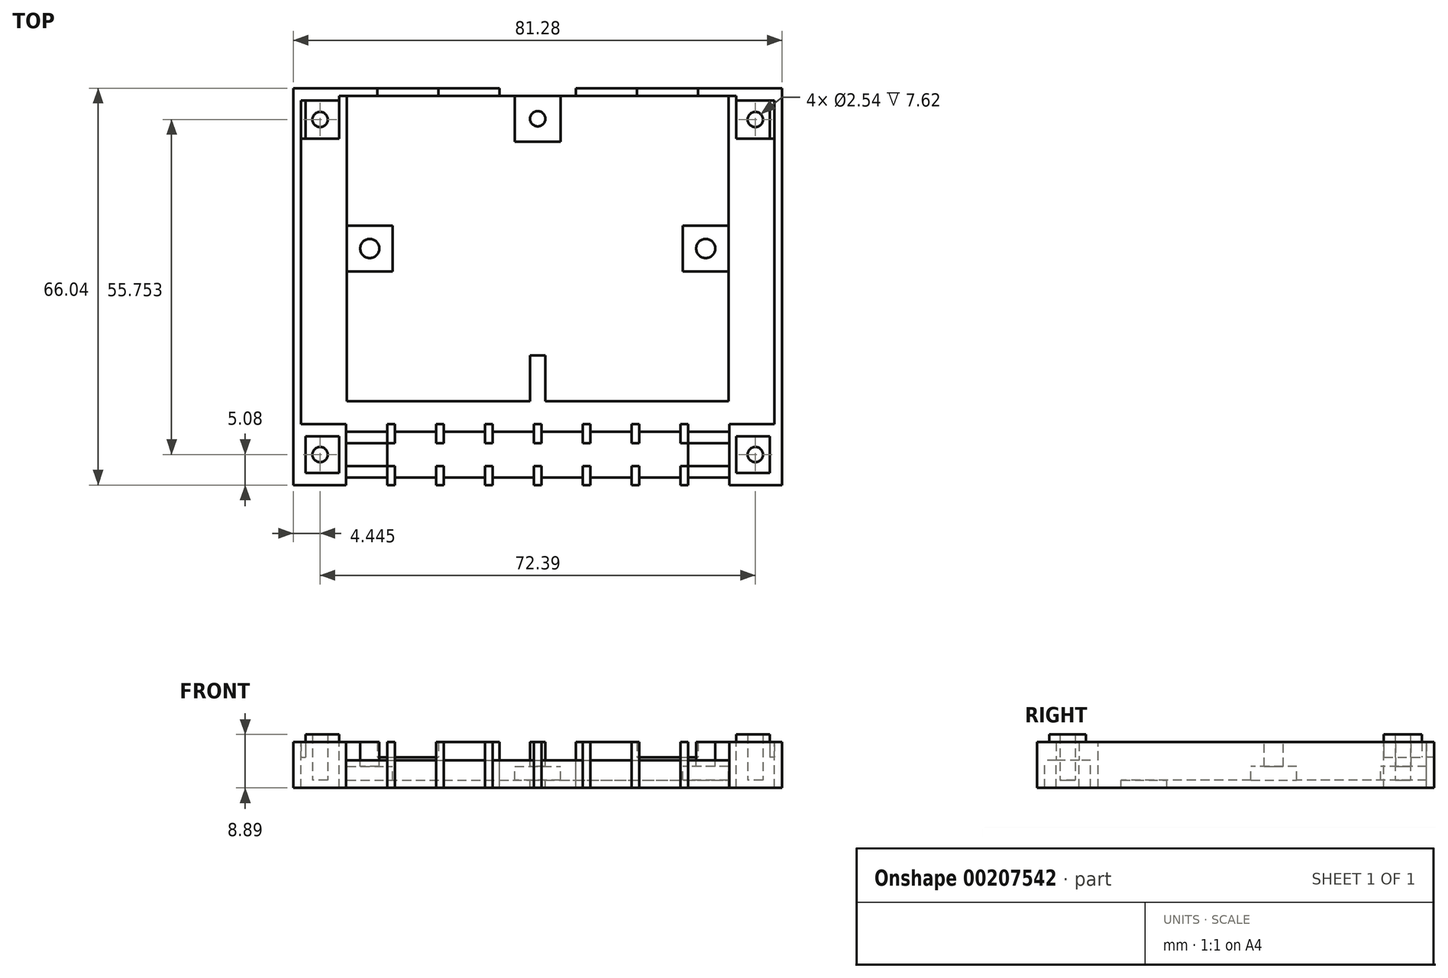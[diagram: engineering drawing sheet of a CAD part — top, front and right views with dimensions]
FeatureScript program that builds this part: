
annotation { "Feature Type Name" : "Feature", "Feature Type Description" : "" }
export const myFeature = defineFeature(function(context is Context, id is Id, definition is map)
    precondition{}
    {
        {
            var Q0;
            Q0=qCreatedBy(makeId("Top.planeOp"),FACE);
            var sketch = newSketch(context, id + "F0", { "sketchPlane" : qUnion([Q0])});
            skLineSegment(sketch, "E0.bottom", {"start": v(-31.75, 25.4) * mm, "end": v(31.75, 25.4) * mm});
            skLineSegment(sketch, "E0.top", {"start": v(-31.75, -25.4) * mm, "end": v(31.75, -25.4) * mm});
            skLineSegment(sketch, "E0.left", {"start": v(-31.75, 25.4) * mm, "end": v(-31.75, -25.4) * mm});
            skLineSegment(sketch, "E0.right", {"start": v(31.75, 25.4) * mm, "end": v(31.75, -25.4) * mm});
            skPoint(sketch, "E0.middle", {"position": v(0, 0) * mm});
            skCircle(sketch, "E1", {"center": v(-27.94, 0) * mm, "radius": 1.59 * mm});
            skCircle(sketch, "E2", {"center": v(27.94, 0) * mm, "radius": 1.59 * mm});
            skCircle(sketch, "E3", {"center": v(0, 21.59) * mm, "radius": 1.27 * mm});
            skLineSegment(sketch, "E4.bottom", {"start": v(-16.51, 32.39) * mm, "end": v(-26.67, 32.38) * mm});
            skLineSegment(sketch, "E4.top", {"start": v(-16.5, 12.07) * mm, "end": v(-26.67, 12.06) * mm});
            skLineSegment(sketch, "E4.left", {"start": v(-16.51, 32.39) * mm, "end": v(-16.5, 12.07) * mm});
            skLineSegment(sketch, "E4.right", {"start": v(-26.67, 32.38) * mm, "end": v(-26.67, 12.06) * mm});
            skPoint(sketch, "E4.middle", {"position": v(-21.59, 22.23) * mm});
            skLineSegment(sketch, "E5.bottom", {"start": v(26.67, 32.39) * mm, "end": v(16.5, 32.39) * mm});
            skLineSegment(sketch, "E5.top", {"start": v(26.67, 12.07) * mm, "end": v(16.5, 12.07) * mm});
            skLineSegment(sketch, "E5.left", {"start": v(26.67, 32.39) * mm, "end": v(26.67, 12.07) * mm});
            skLineSegment(sketch, "E5.right", {"start": v(16.5, 32.38) * mm, "end": v(16.5, 12.07) * mm});
            skPoint(sketch, "E5.middle", {"position": v(21.6, 22.23) * mm});
            skLineSegment(sketch, "E6.bottom", {"start": v(-39.37, 25.4) * mm, "end": v(39.37, 25.4) * mm});
            skLineSegment(sketch, "E6.top", {"start": v(-39.37, -29.21) * mm, "end": v(39.37, -29.21) * mm});
            skLineSegment(sketch, "E6.left", {"start": v(-39.37, 25.4) * mm, "end": v(-39.37, -29.2) * mm});
            skLineSegment(sketch, "E6.right", {"start": v(39.37, 25.4) * mm, "end": v(39.37, -29.2) * mm});
            skLineSegment(sketch, "E7.bottom", {"start": v(-40.64, 26.67) * mm, "end": v(40.64, 26.67) * mm});
            skLineSegment(sketch, "E7.top", {"start": v(-40.64, -39.37) * mm, "end": v(40.64, -39.37) * mm});
            skLineSegment(sketch, "E7.left", {"start": v(-40.64, 26.67) * mm, "end": v(-40.64, -39.37) * mm});
            skLineSegment(sketch, "E7.right", {"start": v(40.64, 26.67) * mm, "end": v(40.64, -39.37) * mm});
            skLineSegment(sketch, "E8.bottom", {"start": v(-39.37, -30.48) * mm, "end": v(39.37, -30.48) * mm});
            skLineSegment(sketch, "E8.top", {"start": v(-39.37, -38.1) * mm, "end": v(39.37, -38.1) * mm});
            skLineSegment(sketch, "E8.left", {"start": v(-39.37, -30.48) * mm, "end": v(-39.37, -38.1) * mm});
            skLineSegment(sketch, "E8.right", {"start": v(39.37, -30.48) * mm, "end": v(39.37, -38.1) * mm});
            skLineSegment(sketch, "E9.bottom", {"start": v(-31.88, -29.21) * mm, "end": v(-25.02, -29.21) * mm});
            skLineSegment(sketch, "E9.top", {"start": v(-31.88, -39.37) * mm, "end": v(-25.02, -39.37) * mm});
            skLineSegment(sketch, "E9.left", {"start": v(-31.88, -29.21) * mm, "end": v(-31.88, -39.37) * mm});
            skLineSegment(sketch, "E9.right", {"start": v(-25.02, -29.21) * mm, "end": v(-25.02, -39.37) * mm});
            skLineSegment(sketch, "E10.1.0.0", {"start": v(-23.75, -29.21) * mm, "end": v(-16.9, -29.21) * mm});
            skLineSegment(sketch, "E10.1.0.1", {"start": v(-23.75, -29.21) * mm, "end": v(-23.75, -39.37) * mm});
            skLineSegment(sketch, "E10.1.0.2", {"start": v(-23.75, -39.37) * mm, "end": v(-16.9, -39.37) * mm});
            skLineSegment(sketch, "E10.1.0.3", {"start": v(-16.9, -29.21) * mm, "end": v(-16.9, -39.37) * mm});
            skLineSegment(sketch, "E10.2.0.0", {"start": v(-15.62, -29.21) * mm, "end": v(-8.76, -29.21) * mm});
            skLineSegment(sketch, "E10.2.0.1", {"start": v(-15.62, -29.21) * mm, "end": v(-15.62, -39.37) * mm});
            skLineSegment(sketch, "E10.2.0.2", {"start": v(-15.62, -39.37) * mm, "end": v(-8.76, -39.37) * mm});
            skLineSegment(sketch, "E10.2.0.3", {"start": v(-8.76, -29.21) * mm, "end": v(-8.76, -39.37) * mm});
            skLineSegment(sketch, "E10.direction1", {"start": v(-31.88, -29.21) * mm, "end": v(-23.75, -29.21) * mm, "construction": true});
            skLineSegment(sketch, "E11.0.3.0", {"start": v(-7.5, -29.21) * mm, "end": v(-0.63, -29.21) * mm});
            skLineSegment(sketch, "E11.3.3.0", {"start": v(-7.5, -29.21) * mm, "end": v(-7.5, -39.37) * mm});
            skLineSegment(sketch, "E11.6.3.0", {"start": v(-7.5, -39.37) * mm, "end": v(-0.64, -39.37) * mm});
            skLineSegment(sketch, "E11.9.3.0", {"start": v(-0.63, -29.21) * mm, "end": v(-0.63, -39.37) * mm});
            skLineSegment(sketch, "E11.0.4.0", {"start": v(0.64, -29.21) * mm, "end": v(7.5, -29.21) * mm});
            skLineSegment(sketch, "E11.3.4.0", {"start": v(0.63, -29.21) * mm, "end": v(0.64, -39.37) * mm});
            skLineSegment(sketch, "E11.6.4.0", {"start": v(0.63, -39.37) * mm, "end": v(7.5, -39.37) * mm});
            skLineSegment(sketch, "E11.9.4.0", {"start": v(7.5, -29.21) * mm, "end": v(7.5, -39.37) * mm});
            skLineSegment(sketch, "E11.0.5.0", {"start": v(8.76, -29.21) * mm, "end": v(15.62, -29.21) * mm});
            skLineSegment(sketch, "E11.3.5.0", {"start": v(8.76, -29.21) * mm, "end": v(8.76, -39.37) * mm});
            skLineSegment(sketch, "E11.6.5.0", {"start": v(8.76, -39.37) * mm, "end": v(15.62, -39.37) * mm});
            skLineSegment(sketch, "E11.9.5.0", {"start": v(15.62, -29.21) * mm, "end": v(15.62, -39.37) * mm});
            skLineSegment(sketch, "E11.0.6.0", {"start": v(16.9, -29.21) * mm, "end": v(23.75, -29.21) * mm});
            skLineSegment(sketch, "E11.3.6.0", {"start": v(16.9, -29.21) * mm, "end": v(16.9, -39.37) * mm});
            skLineSegment(sketch, "E11.6.6.0", {"start": v(16.9, -39.37) * mm, "end": v(23.75, -39.37) * mm});
            skLineSegment(sketch, "E11.9.6.0", {"start": v(23.75, -29.21) * mm, "end": v(23.75, -39.37) * mm});
            skLineSegment(sketch, "E11.0.7.0", {"start": v(25.02, -29.21) * mm, "end": v(31.88, -29.21) * mm});
            skLineSegment(sketch, "E11.3.7.0", {"start": v(25.02, -29.21) * mm, "end": v(25.02, -39.37) * mm});
            skLineSegment(sketch, "E11.6.7.0", {"start": v(25.02, -39.37) * mm, "end": v(31.88, -39.37) * mm});
            skLineSegment(sketch, "E11.9.7.0", {"start": v(31.88, -29.21) * mm, "end": v(31.88, -39.37) * mm});
            skLineSegment(sketch, "E12.bottom", {"start": v(-31.75, -3.8) * mm, "end": v(-24.13, -3.8) * mm});
            skLineSegment(sketch, "E12.top", {"start": v(-31.75, 3.81) * mm, "end": v(-24.13, 3.81) * mm});
            skLineSegment(sketch, "E12.left", {"start": v(-31.75, -3.8) * mm, "end": v(-31.75, 3.81) * mm});
            skLineSegment(sketch, "E12.right", {"start": v(-24.13, -3.8) * mm, "end": v(-24.13, 3.81) * mm});
            skLineSegment(sketch, "E13.bottom", {"start": v(31.75, -3.8) * mm, "end": v(24.13, -3.8) * mm});
            skLineSegment(sketch, "E13.top", {"start": v(31.75, 3.81) * mm, "end": v(24.13, 3.81) * mm});
            skLineSegment(sketch, "E13.left", {"start": v(31.75, -3.8) * mm, "end": v(31.75, 3.81) * mm});
            skLineSegment(sketch, "E13.right", {"start": v(24.13, -3.8) * mm, "end": v(24.13, 3.81) * mm});
            skPoint(sketch, "E13.cornerSnap0", {"position": v(-27.94, -3.8) * mm});
            skLineSegment(sketch, "E14.bottom", {"start": v(3.8, 25.4) * mm, "end": v(-3.81, 25.4) * mm});
            skLineSegment(sketch, "E14.top", {"start": v(3.8, 17.78) * mm, "end": v(-3.81, 17.78) * mm});
            skLineSegment(sketch, "E14.left", {"start": v(3.8, 25.4) * mm, "end": v(3.8, 17.78) * mm});
            skLineSegment(sketch, "E14.right", {"start": v(-3.81, 25.4) * mm, "end": v(-3.81, 17.78) * mm});
            skLineSegment(sketch, "E15.bottom", {"start": v(-1.27, -25.4) * mm, "end": v(1.27, -25.4) * mm});
            skLineSegment(sketch, "E15.top", {"start": v(-1.27, -17.78) * mm, "end": v(1.27, -17.78) * mm});
            skLineSegment(sketch, "E15.left", {"start": v(-1.27, -25.4) * mm, "end": v(-1.27, -17.78) * mm});
            skLineSegment(sketch, "E15.right", {"start": v(1.27, -25.4) * mm, "end": v(1.27, -17.78) * mm});
            skPoint(sketch, "E15.middle", {"position": v(0, -21.59) * mm});
            skCircle(sketch, "E16", {"center": v(-36.2, -34.3) * mm, "radius": 1.27 * mm});
            skCircle(sketch, "E17", {"center": v(36.2, -34.3) * mm, "radius": 1.27 * mm});
            skLineSegment(sketch, "E18.bottom", {"start": v(-31.88, -32.39) * mm, "end": v(31.88, -32.39) * mm});
            skLineSegment(sketch, "E18.top", {"start": v(-31.88, -36.2) * mm, "end": v(31.88, -36.2) * mm});
            skLineSegment(sketch, "E18.left", {"start": v(-31.88, -32.39) * mm, "end": v(-31.88, -36.2) * mm});
            skLineSegment(sketch, "E18.right", {"start": v(31.88, -32.39) * mm, "end": v(31.88, -36.2) * mm});
            skLineSegment(sketch, "E19.bottom", {"start": v(-6.35, 26.67) * mm, "end": v(6.35, 26.67) * mm});
            skLineSegment(sketch, "E19.top", {"start": v(-6.35, 25.4) * mm, "end": v(6.35, 25.4) * mm});
            skLineSegment(sketch, "E19.left", {"start": v(-6.35, 26.67) * mm, "end": v(-6.35, 25.4) * mm});
            skLineSegment(sketch, "E19.right", {"start": v(6.35, 26.67) * mm, "end": v(6.35, 25.4) * mm});
            skLineSegment(sketch, "E20.bottom", {"start": v(-39.37, 24.64) * mm, "end": v(-33.02, 24.64) * mm});
            skLineSegment(sketch, "E20.top", {"start": v(-39.37, 18.29) * mm, "end": v(-33.02, 18.29) * mm});
            skLineSegment(sketch, "E20.left", {"start": v(-39.37, 24.64) * mm, "end": v(-39.37, 18.29) * mm});
            skLineSegment(sketch, "E20.right", {"start": v(-33.02, 24.64) * mm, "end": v(-33.02, 18.29) * mm});
            skLineSegment(sketch, "E21.bottom", {"start": v(39.37, 24.64) * mm, "end": v(33.02, 24.64) * mm});
            skLineSegment(sketch, "E21.top", {"start": v(39.37, 18.29) * mm, "end": v(33.02, 18.29) * mm});
            skLineSegment(sketch, "E21.left", {"start": v(39.37, 24.64) * mm, "end": v(39.37, 18.29) * mm});
            skLineSegment(sketch, "E21.right", {"start": v(33.02, 24.64) * mm, "end": v(33.02, 18.29) * mm});
            skLineSegment(sketch, "E22.bottom", {"start": v(-38.6, -31.24) * mm, "end": v(-33.02, -31.24) * mm});
            skLineSegment(sketch, "E22.top", {"start": v(-38.6, -37.34) * mm, "end": v(-33.02, -37.34) * mm});
            skLineSegment(sketch, "E22.left", {"start": v(-38.6, -31.24) * mm, "end": v(-38.6, -37.34) * mm});
            skLineSegment(sketch, "E22.right", {"start": v(-33.02, -31.24) * mm, "end": v(-33.02, -37.34) * mm});
            skLineSegment(sketch, "E23.bottom", {"start": v(33.02, -31.24) * mm, "end": v(38.6, -31.24) * mm});
            skLineSegment(sketch, "E23.top", {"start": v(33.02, -37.34) * mm, "end": v(38.6, -37.34) * mm});
            skLineSegment(sketch, "E23.left", {"start": v(33.02, -31.24) * mm, "end": v(33.02, -37.34) * mm});
            skLineSegment(sketch, "E23.right", {"start": v(38.6, -31.24) * mm, "end": v(38.6, -37.34) * mm});
            skPoint(sketch, "E24", {"position": v(-36.2, 21.46) * mm});
            skPoint(sketch, "E24.positionSnap0", {"position": v(-39.37, 21.46) * mm});
            skPoint(sketch, "E25", {"position": v(36.2, 21.46) * mm});
            skLineSegment(sketch, "E26", {"start": v(-33.02, 24.64) * mm, "end": v(-33.02, 25.4) * mm});
            skLineSegment(sketch, "E27", {"start": v(33.02, 24.64) * mm, "end": v(33.02, 25.4) * mm});
            skLineSegment(sketch, "E28", {"start": v(-38.6, 18.29) * mm, "end": v(-38.6, 24.64) * mm});
            skLineSegment(sketch, "E29", {"start": v(38.6, 18.29) * mm, "end": v(38.6, 24.64) * mm});
            skCircle(sketch, "E30", {"center": v(-36.2, 21.46) * mm, "radius": 1.27 * mm});
            skCircle(sketch, "E31", {"center": v(36.2, 21.46) * mm, "radius": 1.27 * mm});
            skSolve(sketch);
        }
        {
            var Q0;
            {var subQ0=sQuery(id+"F0.wireOp",EDGE,"E18.bottom");var subQ1=sQuery(id+"F0.wireOp",EDGE,"E11.3.4.0");var subQ2=makeQuery(id+"F0.imprint","INTERSECT",VERTEX,{"derivedFrom":[subQ1,subQ0]});Q0=makeQuery(id+"F0.imprint","IMPRINT",FACE,{"disambiguationData":[TD([[makeQuery(id+"F0.imprint","IMPRINT",EDGE,{"disambiguationData":[TD([[subQ2,-1.0]])],"derivedFrom":subQ1}),1.0]])]});}
            var Q1;
            {var subQ0=sQuery(id+"F0.wireOp",EDGE,"E10.1.0.1");var subQ1=sQuery(id+"F0.wireOp",EDGE,"E8.bottom");var subQ2=makeQuery(id+"F0.imprint","INTERSECT",VERTEX,{"derivedFrom":[subQ1,subQ0]});Q1=makeQuery(id+"F0.imprint","IMPRINT",FACE,{"disambiguationData":[TD([[makeQuery(id+"F0.imprint","IMPRINT",EDGE,{"disambiguationData":[TD([[subQ2,-1.0]])],"derivedFrom":subQ1}),-1.0]])]});}
            var Q2;
            {var subQ5=sQuery(id+"F0.wireOp",EDGE,"E18.right");Q2=makeQuery(id+"F0.imprint","IMPRINT",FACE,{"disambiguationData":[TD([[makeQuery(id+"F0.imprint","IMPRINT",EDGE,{"derivedFrom":subQ5}),-1.0]])]});}
            var Q3;
            {var subQ0=sQuery(id+"F0.wireOp",EDGE,"E11.3.4.0");var subQ1=sQuery(id+"F0.wireOp",EDGE,"E8.top");var subQ2=makeQuery(id+"F0.imprint","INTERSECT",VERTEX,{"derivedFrom":[subQ1,subQ0]});Q3=makeQuery(id+"F0.imprint","IMPRINT",FACE,{"disambiguationData":[TD([[makeQuery(id+"F0.imprint","IMPRINT",EDGE,{"disambiguationData":[TD([[subQ2,-1.0]])],"derivedFrom":subQ1}),1.0]])]});}
            var Q4;
            {var subQ0=sQuery(id+"F0.wireOp",EDGE,"E11.3.3.0");var subQ1=sQuery(id+"F0.wireOp",EDGE,"E8.top");var subQ2=makeQuery(id+"F0.imprint","INTERSECT",VERTEX,{"derivedFrom":[subQ1,subQ0]});Q4=makeQuery(id+"F0.imprint","IMPRINT",FACE,{"disambiguationData":[TD([[makeQuery(id+"F0.imprint","IMPRINT",EDGE,{"disambiguationData":[TD([[subQ2,-1.0]])],"derivedFrom":subQ1}),1.0]])]});}
            var Q5;
            {var subQ0=sQuery(id+"F0.wireOp",EDGE,"E18.bottom");var subQ1=sQuery(id+"F0.wireOp",EDGE,"E11.9.3.0");var subQ2=makeQuery(id+"F0.imprint","INTERSECT",VERTEX,{"derivedFrom":[subQ1,subQ0]});Q5=makeQuery(id+"F0.imprint","IMPRINT",FACE,{"disambiguationData":[TD([[makeQuery(id+"F0.imprint","IMPRINT",EDGE,{"disambiguationData":[TD([[subQ2,-1.0]])],"derivedFrom":subQ1}),1.0]])]});}
            var Q6;
            {var subQ0=sQuery(id+"F0.wireOp",EDGE,"E11.3.4.0");var subQ1=sQuery(id+"F0.wireOp",EDGE,"E8.bottom");var subQ2=makeQuery(id+"F0.imprint","INTERSECT",VERTEX,{"derivedFrom":[subQ1,subQ0]});Q6=makeQuery(id+"F0.imprint","IMPRINT",FACE,{"disambiguationData":[TD([[makeQuery(id+"F0.imprint","IMPRINT",EDGE,{"disambiguationData":[TD([[subQ2,-1.0]])],"derivedFrom":subQ1}),-1.0]])]});}
            var Q7;
            {var subQ0=sQuery(id+"F0.wireOp",EDGE,"E18.bottom");var subQ1=sQuery(id+"F0.wireOp",EDGE,"E11.3.3.0");var subQ2=makeQuery(id+"F0.imprint","INTERSECT",VERTEX,{"derivedFrom":[subQ1,subQ0]});Q7=makeQuery(id+"F0.imprint","IMPRINT",FACE,{"disambiguationData":[TD([[makeQuery(id+"F0.imprint","IMPRINT",EDGE,{"disambiguationData":[TD([[subQ2,-1.0]])],"derivedFrom":subQ1}),1.0]])]});}
            var Q8;
            {var subQ0=sQuery(id+"F0.wireOp",EDGE,"E5.top");Q8=makeQuery(id+"F0.imprint","IMPRINT",FACE,{"disambiguationData":[TD([[makeQuery(id+"F0.imprint","IMPRINT",EDGE,{"derivedFrom":subQ0}),-1.0]])]});}
            var Q9;
            {var subQ0=sQuery(id+"F0.wireOp",EDGE,"E4.top");Q9=makeQuery(id+"F0.imprint","IMPRINT",FACE,{"disambiguationData":[TD([[makeQuery(id+"F0.imprint","IMPRINT",EDGE,{"derivedFrom":subQ0}),-1.0]])]});}
            var Q10;
            Q10=makeQuery(id+"F0.imprint","IMPRINT",FACE,{"disambiguationData":[TD([[makeQuery(id+"F0.imprint","IMPRINT",EDGE,{"derivedFrom":sQuery(id+"F0.wireOp",EDGE,"E1")}),-1.0]])]});
            var Q11;
            Q11=makeQuery(id+"F0.imprint","IMPRINT",FACE,{"disambiguationData":[TD([[makeQuery(id+"F0.imprint","IMPRINT",EDGE,{"derivedFrom":sQuery(id+"F0.wireOp",EDGE,"E2")}),-1.0]])]});
            var Q12;
            {var subQ0=sQuery(id+"F0.wireOp",EDGE,"E10.2.0.1");var subQ1=sQuery(id+"F0.wireOp",EDGE,"E8.top");var subQ2=makeQuery(id+"F0.imprint","INTERSECT",VERTEX,{"derivedFrom":[subQ1,subQ0]});Q12=makeQuery(id+"F0.imprint","IMPRINT",FACE,{"disambiguationData":[TD([[makeQuery(id+"F0.imprint","IMPRINT",EDGE,{"disambiguationData":[TD([[subQ2,-1.0]])],"derivedFrom":subQ1}),1.0]])]});}
            var Q13;
            {var subQ23=sQuery(id+"F0.wireOp",EDGE,"E4.top");Q13=makeQuery(id+"F0.imprint","IMPRINT",FACE,{"disambiguationData":[TD([[makeQuery(id+"F0.imprint","IMPRINT",EDGE,{"derivedFrom":subQ23}),1.0]])]});}
            var Q14;
            {var subQ0=sQuery(id+"F0.wireOp",EDGE,"E11.3.3.0");var subQ1=sQuery(id+"F0.wireOp",EDGE,"E8.bottom");var subQ2=makeQuery(id+"F0.imprint","INTERSECT",VERTEX,{"derivedFrom":[subQ1,subQ0]});Q14=makeQuery(id+"F0.imprint","IMPRINT",FACE,{"disambiguationData":[TD([[makeQuery(id+"F0.imprint","IMPRINT",EDGE,{"disambiguationData":[TD([[subQ2,-1.0]])],"derivedFrom":subQ1}),-1.0]])]});}
            var Q15;
            {var subQ0=sQuery(id+"F0.wireOp",EDGE,"E10.1.0.3");var subQ1=sQuery(id+"F0.wireOp",EDGE,"E8.top");var subQ2=makeQuery(id+"F0.imprint","INTERSECT",VERTEX,{"derivedFrom":[subQ1,subQ0]});Q15=makeQuery(id+"F0.imprint","IMPRINT",FACE,{"disambiguationData":[TD([[makeQuery(id+"F0.imprint","IMPRINT",EDGE,{"disambiguationData":[TD([[subQ2,-1.0]])],"derivedFrom":subQ1}),1.0]])]});}
            var Q16;
            {var subQ0=sQuery(id+"F0.wireOp",EDGE,"E18.bottom");var subQ1=sQuery(id+"F0.wireOp",EDGE,"E10.2.0.1");var subQ2=makeQuery(id+"F0.imprint","INTERSECT",VERTEX,{"derivedFrom":[subQ1,subQ0]});Q16=makeQuery(id+"F0.imprint","IMPRINT",FACE,{"disambiguationData":[TD([[makeQuery(id+"F0.imprint","IMPRINT",EDGE,{"disambiguationData":[TD([[subQ2,-1.0]])],"derivedFrom":subQ1}),1.0]])]});}
            var Q17;
            {var subQ11=sQuery(id+"F0.wireOp",EDGE,"E7.right");Q17=makeQuery(id+"F0.imprint","IMPRINT",FACE,{"disambiguationData":[TD([[makeQuery(id+"F0.imprint","IMPRINT",EDGE,{"derivedFrom":subQ11}),-1.0]])]});}
            var Q18;
            {var subQ0=sQuery(id+"F0.wireOp",EDGE,"E10.1.0.1");var subQ1=sQuery(id+"F0.wireOp",EDGE,"E8.top");var subQ2=makeQuery(id+"F0.imprint","INTERSECT",VERTEX,{"derivedFrom":[subQ1,subQ0]});Q18=makeQuery(id+"F0.imprint","IMPRINT",FACE,{"disambiguationData":[TD([[makeQuery(id+"F0.imprint","IMPRINT",EDGE,{"disambiguationData":[TD([[subQ2,-1.0]])],"derivedFrom":subQ1}),1.0]])]});}
            var Q19;
            {var subQ0=sQuery(id+"F0.wireOp",EDGE,"E18.bottom");var subQ1=sQuery(id+"F0.wireOp",EDGE,"E10.1.0.1");var subQ2=makeQuery(id+"F0.imprint","INTERSECT",VERTEX,{"derivedFrom":[subQ1,subQ0]});Q19=makeQuery(id+"F0.imprint","IMPRINT",FACE,{"disambiguationData":[TD([[makeQuery(id+"F0.imprint","IMPRINT",EDGE,{"disambiguationData":[TD([[subQ2,-1.0]])],"derivedFrom":subQ1}),1.0]])]});}
            var Q20;
            {var subQ0=sQuery(id+"F0.wireOp",EDGE,"E8.right");Q20=makeQuery(id+"F0.imprint","IMPRINT",FACE,{"disambiguationData":[TD([[makeQuery(id+"F0.imprint","IMPRINT",EDGE,{"derivedFrom":subQ0}),-1.0]])]});}
            var Q21;
            {var subQ0=sQuery(id+"F0.wireOp",EDGE,"E10.2.0.1");var subQ1=sQuery(id+"F0.wireOp",EDGE,"E8.bottom");var subQ2=makeQuery(id+"F0.imprint","INTERSECT",VERTEX,{"derivedFrom":[subQ1,subQ0]});Q21=makeQuery(id+"F0.imprint","IMPRINT",FACE,{"disambiguationData":[TD([[makeQuery(id+"F0.imprint","IMPRINT",EDGE,{"disambiguationData":[TD([[subQ2,-1.0]])],"derivedFrom":subQ1}),-1.0]])]});}
            var Q22;
            {var subQ5=sQuery(id+"F0.wireOp",EDGE,"E11.6.5.0");Q22=makeQuery(id+"F0.imprint","IMPRINT",FACE,{"disambiguationData":[TD([[makeQuery(id+"F0.imprint","IMPRINT",EDGE,{"derivedFrom":subQ5}),1.0]])]});}
            var Q23;
            {var subQ5=sQuery(id+"F0.wireOp",EDGE,"E11.6.7.0");Q23=makeQuery(id+"F0.imprint","IMPRINT",FACE,{"disambiguationData":[TD([[makeQuery(id+"F0.imprint","IMPRINT",EDGE,{"derivedFrom":subQ5}),1.0]])]});}
            var Q24;
            {var subQ0=sQuery(id+"F0.wireOp",EDGE,"E11.3.7.0");var subQ1=sQuery(id+"F0.wireOp",EDGE,"E8.bottom");var subQ2=makeQuery(id+"F0.imprint","INTERSECT",VERTEX,{"derivedFrom":[subQ1,subQ0]});Q24=makeQuery(id+"F0.imprint","IMPRINT",FACE,{"disambiguationData":[TD([[makeQuery(id+"F0.imprint","IMPRINT",EDGE,{"disambiguationData":[TD([[subQ2,-1.0]])],"derivedFrom":subQ1}),-1.0]])]});}
            var Q25;
            {var subQ0=sQuery(id+"F0.wireOp",EDGE,"E18.bottom");var subQ1=sQuery(id+"F0.wireOp",EDGE,"E9.right");var subQ2=makeQuery(id+"F0.imprint","INTERSECT",VERTEX,{"derivedFrom":[subQ1,subQ0]});Q25=makeQuery(id+"F0.imprint","IMPRINT",FACE,{"disambiguationData":[TD([[makeQuery(id+"F0.imprint","IMPRINT",EDGE,{"disambiguationData":[TD([[subQ2,-1.0]])],"derivedFrom":subQ1}),1.0]])]});}
            var Q26;
            {var subQ5=sQuery(id+"F0.wireOp",EDGE,"E11.6.6.0");Q26=makeQuery(id+"F0.imprint","IMPRINT",FACE,{"disambiguationData":[TD([[makeQuery(id+"F0.imprint","IMPRINT",EDGE,{"derivedFrom":subQ5}),1.0]])]});}
            var Q27;
            Q27=makeQuery(id+"F0.imprint","IMPRINT",FACE,{"disambiguationData":[TD([[makeQuery(id+"F0.imprint","IMPRINT",EDGE,{"derivedFrom":sQuery(id+"F0.wireOp",EDGE,"E3")}),-1.0]])]});
            var Q28;
            {var subQ0=sQuery(id+"F0.wireOp",EDGE,"E11.3.7.0");var subQ1=sQuery(id+"F0.wireOp",EDGE,"E8.top");var subQ2=makeQuery(id+"F0.imprint","INTERSECT",VERTEX,{"derivedFrom":[subQ1,subQ0]});Q28=makeQuery(id+"F0.imprint","IMPRINT",FACE,{"disambiguationData":[TD([[makeQuery(id+"F0.imprint","IMPRINT",EDGE,{"disambiguationData":[TD([[subQ2,-1.0]])],"derivedFrom":subQ1}),1.0]])]});}
            var Q29;
            {var subQ0=sQuery(id+"F0.wireOp",EDGE,"E11.3.5.0");var subQ1=sQuery(id+"F0.wireOp",EDGE,"E8.top");var subQ2=makeQuery(id+"F0.imprint","INTERSECT",VERTEX,{"derivedFrom":[subQ1,subQ0]});Q29=makeQuery(id+"F0.imprint","IMPRINT",FACE,{"disambiguationData":[TD([[makeQuery(id+"F0.imprint","IMPRINT",EDGE,{"disambiguationData":[TD([[subQ2,-1.0]])],"derivedFrom":subQ1}),1.0]])]});}
            var Q30;
            {var subQ0=sQuery(id+"F0.wireOp",EDGE,"E18.bottom");var subQ1=sQuery(id+"F0.wireOp",EDGE,"E11.9.5.0");var subQ2=makeQuery(id+"F0.imprint","INTERSECT",VERTEX,{"derivedFrom":[subQ1,subQ0]});Q30=makeQuery(id+"F0.imprint","IMPRINT",FACE,{"disambiguationData":[TD([[makeQuery(id+"F0.imprint","IMPRINT",EDGE,{"disambiguationData":[TD([[subQ2,-1.0]])],"derivedFrom":subQ1}),1.0]])]});}
            var Q31;
            {var subQ5=sQuery(id+"F0.wireOp",EDGE,"E10.2.0.2");Q31=makeQuery(id+"F0.imprint","IMPRINT",FACE,{"disambiguationData":[TD([[makeQuery(id+"F0.imprint","IMPRINT",EDGE,{"derivedFrom":subQ5}),1.0]])]});}
            var Q32;
            {var subQ0=sQuery(id+"F0.wireOp",EDGE,"E9.left");var subQ1=sQuery(id+"F0.wireOp",EDGE,"E8.bottom");var subQ2=makeQuery(id+"F0.imprint","INTERSECT",VERTEX,{"derivedFrom":[subQ1,subQ0]});Q32=makeQuery(id+"F0.imprint","IMPRINT",FACE,{"disambiguationData":[TD([[makeQuery(id+"F0.imprint","IMPRINT",EDGE,{"disambiguationData":[TD([[subQ2,-1.0]])],"derivedFrom":subQ1}),-1.0]])]});}
            var Q33;
            {var subQ5=sQuery(id+"F0.wireOp",EDGE,"E11.6.4.0");Q33=makeQuery(id+"F0.imprint","IMPRINT",FACE,{"disambiguationData":[TD([[makeQuery(id+"F0.imprint","IMPRINT",EDGE,{"derivedFrom":subQ5}),1.0]])]});}
            var Q34;
            {var subQ0=sQuery(id+"F0.wireOp",EDGE,"E11.3.6.0");var subQ1=sQuery(id+"F0.wireOp",EDGE,"E8.bottom");var subQ2=makeQuery(id+"F0.imprint","INTERSECT",VERTEX,{"derivedFrom":[subQ1,subQ0]});Q34=makeQuery(id+"F0.imprint","IMPRINT",FACE,{"disambiguationData":[TD([[makeQuery(id+"F0.imprint","IMPRINT",EDGE,{"disambiguationData":[TD([[subQ2,-1.0]])],"derivedFrom":subQ1}),-1.0]])]});}
            var Q35;
            {var subQ0=sQuery(id+"F0.wireOp",EDGE,"E11.3.6.0");var subQ1=sQuery(id+"F0.wireOp",EDGE,"E8.top");var subQ2=makeQuery(id+"F0.imprint","INTERSECT",VERTEX,{"derivedFrom":[subQ1,subQ0]});Q35=makeQuery(id+"F0.imprint","IMPRINT",FACE,{"disambiguationData":[TD([[makeQuery(id+"F0.imprint","IMPRINT",EDGE,{"disambiguationData":[TD([[subQ2,-1.0]])],"derivedFrom":subQ1}),1.0]])]});}
            var Q36;
            {var subQ0=sQuery(id+"F0.wireOp",EDGE,"E18.bottom");var subQ1=sQuery(id+"F0.wireOp",EDGE,"E11.3.5.0");var subQ2=makeQuery(id+"F0.imprint","INTERSECT",VERTEX,{"derivedFrom":[subQ1,subQ0]});Q36=makeQuery(id+"F0.imprint","IMPRINT",FACE,{"disambiguationData":[TD([[makeQuery(id+"F0.imprint","IMPRINT",EDGE,{"disambiguationData":[TD([[subQ2,-1.0]])],"derivedFrom":subQ1}),1.0]])]});}
            var Q37;
            {var subQ5=sQuery(id+"F0.wireOp",EDGE,"E10.1.0.2");Q37=makeQuery(id+"F0.imprint","IMPRINT",FACE,{"disambiguationData":[TD([[makeQuery(id+"F0.imprint","IMPRINT",EDGE,{"derivedFrom":subQ5}),1.0]])]});}
            var Q38;
            {var subQ5=sQuery(id+"F0.wireOp",EDGE,"E9.bottom");Q38=makeQuery(id+"F0.imprint","IMPRINT",FACE,{"disambiguationData":[TD([[makeQuery(id+"F0.imprint","IMPRINT",EDGE,{"derivedFrom":subQ5}),-1.0]])]});}
            var Q39;
            {var subQ0=sQuery(id+"F0.wireOp",EDGE,"E11.3.5.0");var subQ1=sQuery(id+"F0.wireOp",EDGE,"E8.bottom");var subQ2=makeQuery(id+"F0.imprint","INTERSECT",VERTEX,{"derivedFrom":[subQ1,subQ0]});Q39=makeQuery(id+"F0.imprint","IMPRINT",FACE,{"disambiguationData":[TD([[makeQuery(id+"F0.imprint","IMPRINT",EDGE,{"disambiguationData":[TD([[subQ2,-1.0]])],"derivedFrom":subQ1}),-1.0]])]});}
            var Q40;
            {var subQ0=sQuery(id+"F0.wireOp",EDGE,"E18.bottom");var subQ1=sQuery(id+"F0.wireOp",EDGE,"E11.3.6.0");var subQ2=makeQuery(id+"F0.imprint","INTERSECT",VERTEX,{"derivedFrom":[subQ1,subQ0]});Q40=makeQuery(id+"F0.imprint","IMPRINT",FACE,{"disambiguationData":[TD([[makeQuery(id+"F0.imprint","IMPRINT",EDGE,{"disambiguationData":[TD([[subQ2,-1.0]])],"derivedFrom":subQ1}),1.0]])]});}
            var Q41;
            {var subQ5=sQuery(id+"F0.wireOp",EDGE,"E11.6.3.0");Q41=makeQuery(id+"F0.imprint","IMPRINT",FACE,{"disambiguationData":[TD([[makeQuery(id+"F0.imprint","IMPRINT",EDGE,{"derivedFrom":subQ5}),1.0]])]});}
            var Q42;
            {var subQ5=sQuery(id+"F0.wireOp",EDGE,"E11.0.5.0");Q42=makeQuery(id+"F0.imprint","IMPRINT",FACE,{"disambiguationData":[TD([[makeQuery(id+"F0.imprint","IMPRINT",EDGE,{"derivedFrom":subQ5}),-1.0]])]});}
            var Q43;
            {var subQ0=sQuery(id+"F0.wireOp",EDGE,"E18.bottom");var subQ1=sQuery(id+"F0.wireOp",EDGE,"E11.9.4.0");var subQ2=makeQuery(id+"F0.imprint","INTERSECT",VERTEX,{"derivedFrom":[subQ1,subQ0]});Q43=makeQuery(id+"F0.imprint","IMPRINT",FACE,{"disambiguationData":[TD([[makeQuery(id+"F0.imprint","IMPRINT",EDGE,{"disambiguationData":[TD([[subQ2,-1.0]])],"derivedFrom":subQ1}),1.0]])]});}
            var Q44;
            {var subQ0=sQuery(id+"F0.wireOp",EDGE,"E11.9.3.0");var subQ1=sQuery(id+"F0.wireOp",EDGE,"E8.top");var subQ2=makeQuery(id+"F0.imprint","INTERSECT",VERTEX,{"derivedFrom":[subQ1,subQ0]});Q44=makeQuery(id+"F0.imprint","IMPRINT",FACE,{"disambiguationData":[TD([[makeQuery(id+"F0.imprint","IMPRINT",EDGE,{"disambiguationData":[TD([[subQ2,-1.0]])],"derivedFrom":subQ1}),1.0]])]});}
            var Q45;
            {var subQ0=sQuery(id+"F0.wireOp",EDGE,"E11.9.6.0");var subQ1=sQuery(id+"F0.wireOp",EDGE,"E8.bottom");var subQ2=makeQuery(id+"F0.imprint","INTERSECT",VERTEX,{"derivedFrom":[subQ1,subQ0]});Q45=makeQuery(id+"F0.imprint","IMPRINT",FACE,{"disambiguationData":[TD([[makeQuery(id+"F0.imprint","IMPRINT",EDGE,{"disambiguationData":[TD([[subQ2,-1.0]])],"derivedFrom":subQ1}),-1.0]])]});}
            var Q46;
            {var subQ5=sQuery(id+"F0.wireOp",EDGE,"E11.0.4.0");Q46=makeQuery(id+"F0.imprint","IMPRINT",FACE,{"disambiguationData":[TD([[makeQuery(id+"F0.imprint","IMPRINT",EDGE,{"derivedFrom":subQ5}),-1.0]])]});}
            var Q47;
            Q47=makeQuery(id+"F0.imprint","IMPRINT",FACE,{"disambiguationData":[TD([[makeQuery(id+"F0.imprint","IMPRINT",EDGE,{"derivedFrom":sQuery(id+"F0.wireOp",EDGE,"y6P8BbUv-Oivx-0iiG-fBJo-7x3XaV8NzKCm.bottom")}),-1.0]])]});
            var Q48;
            Q48=makeQuery(id+"F0.imprint","IMPRINT",FACE,{"disambiguationData":[TD([[makeQuery(id+"F0.imprint","IMPRINT",EDGE,{"derivedFrom":sQuery(id+"F0.wireOp",EDGE,"E20.bottom")}),-1.0]])]});
            var Q49;
            Q49=makeQuery(id+"F0.imprint","IMPRINT",FACE,{"disambiguationData":[TD([[makeQuery(id+"F0.imprint","IMPRINT",EDGE,{"derivedFrom":sQuery(id+"F0.wireOp",EDGE,"E15.bottom")}),1.0]])]});
            var Q50;
            Q50=makeQuery(id+"F0.imprint","IMPRINT",FACE,{"disambiguationData":[TD([[makeQuery(id+"F0.imprint","IMPRINT",EDGE,{"derivedFrom":sQuery(id+"F0.wireOp",EDGE,"E21.bottom")}),1.0]])]});
            var Q51;
            {var subQ0=sQuery(id+"F0.wireOp",EDGE,"E11.9.3.0");var subQ1=sQuery(id+"F0.wireOp",EDGE,"E8.bottom");var subQ2=makeQuery(id+"F0.imprint","INTERSECT",VERTEX,{"derivedFrom":[subQ1,subQ0]});Q51=makeQuery(id+"F0.imprint","IMPRINT",FACE,{"disambiguationData":[TD([[makeQuery(id+"F0.imprint","IMPRINT",EDGE,{"disambiguationData":[TD([[subQ2,-1.0]])],"derivedFrom":subQ1}),-1.0]])]});}
            var Q52;
            {var subQ0=sQuery(id+"F0.wireOp",EDGE,"E18.bottom");var subQ1=sQuery(id+"F0.wireOp",EDGE,"E10.2.0.3");var subQ2=makeQuery(id+"F0.imprint","INTERSECT",VERTEX,{"derivedFrom":[subQ1,subQ0]});Q52=makeQuery(id+"F0.imprint","IMPRINT",FACE,{"disambiguationData":[TD([[makeQuery(id+"F0.imprint","IMPRINT",EDGE,{"disambiguationData":[TD([[subQ2,-1.0]])],"derivedFrom":subQ1}),1.0]])]});}
            var Q53;
            {var subQ0=sQuery(id+"F0.wireOp",EDGE,"E11.9.5.0");var subQ1=sQuery(id+"F0.wireOp",EDGE,"E8.top");var subQ2=makeQuery(id+"F0.imprint","INTERSECT",VERTEX,{"derivedFrom":[subQ1,subQ0]});Q53=makeQuery(id+"F0.imprint","IMPRINT",FACE,{"disambiguationData":[TD([[makeQuery(id+"F0.imprint","IMPRINT",EDGE,{"disambiguationData":[TD([[subQ2,-1.0]])],"derivedFrom":subQ1}),1.0]])]});}
            var Q54;
            {var subQ5=sQuery(id+"F0.wireOp",EDGE,"E11.0.3.0");Q54=makeQuery(id+"F0.imprint","IMPRINT",FACE,{"disambiguationData":[TD([[makeQuery(id+"F0.imprint","IMPRINT",EDGE,{"derivedFrom":subQ5}),-1.0]])]});}
            var Q55;
            {var subQ0=sQuery(id+"F0.wireOp",EDGE,"E18.bottom");var subQ1=sQuery(id+"F0.wireOp",EDGE,"E10.1.0.3");var subQ2=makeQuery(id+"F0.imprint","INTERSECT",VERTEX,{"derivedFrom":[subQ1,subQ0]});Q55=makeQuery(id+"F0.imprint","IMPRINT",FACE,{"disambiguationData":[TD([[makeQuery(id+"F0.imprint","IMPRINT",EDGE,{"disambiguationData":[TD([[subQ2,-1.0]])],"derivedFrom":subQ1}),1.0]])]});}
            var Q56;
            {var subQ0=sQuery(id+"F0.wireOp",EDGE,"E7.bottom");var subQ1=sQuery(id+"F0.wireOp",EDGE,"E5.left");var subQ2=makeQuery(id+"F0.imprint","INTERSECT",VERTEX,{"derivedFrom":[subQ1,subQ0]});Q56=makeQuery(id+"F0.imprint","IMPRINT",FACE,{"disambiguationData":[TD([[makeQuery(id+"F0.imprint","IMPRINT",EDGE,{"disambiguationData":[TD([[subQ2,-1.0]])],"derivedFrom":subQ1}),-1.0]])]});}
            var Q57;
            {var subQ0=sQuery(id+"F0.wireOp",EDGE,"E9.right");var subQ1=sQuery(id+"F0.wireOp",EDGE,"E8.top");var subQ2=makeQuery(id+"F0.imprint","INTERSECT",VERTEX,{"derivedFrom":[subQ1,subQ0]});Q57=makeQuery(id+"F0.imprint","IMPRINT",FACE,{"disambiguationData":[TD([[makeQuery(id+"F0.imprint","IMPRINT",EDGE,{"disambiguationData":[TD([[subQ2,-1.0]])],"derivedFrom":subQ1}),1.0]])]});}
            var Q58;
            {var subQ0=sQuery(id+"F0.wireOp",EDGE,"E7.bottom");var subQ1=sQuery(id+"F0.wireOp",EDGE,"E4.left");var subQ2=makeQuery(id+"F0.imprint","INTERSECT",VERTEX,{"derivedFrom":[subQ1,subQ0]});Q58=makeQuery(id+"F0.imprint","IMPRINT",FACE,{"disambiguationData":[TD([[makeQuery(id+"F0.imprint","IMPRINT",EDGE,{"disambiguationData":[TD([[subQ2,-1.0]])],"derivedFrom":subQ1}),-1.0]])]});}
            var Q59;
            {var subQ5=sQuery(id+"F0.wireOp",EDGE,"E19.right");Q59=makeQuery(id+"F0.imprint","IMPRINT",FACE,{"disambiguationData":[TD([[makeQuery(id+"F0.imprint","IMPRINT",EDGE,{"derivedFrom":subQ5}),1.0]])]});}
            var Q60;
            {var subQ5=sQuery(id+"F0.wireOp",EDGE,"E10.2.0.0");Q60=makeQuery(id+"F0.imprint","IMPRINT",FACE,{"disambiguationData":[TD([[makeQuery(id+"F0.imprint","IMPRINT",EDGE,{"derivedFrom":subQ5}),-1.0]])]});}
            var Q61;
            {var subQ5=sQuery(id+"F0.wireOp",EDGE,"E19.left");Q61=makeQuery(id+"F0.imprint","IMPRINT",FACE,{"disambiguationData":[TD([[makeQuery(id+"F0.imprint","IMPRINT",EDGE,{"derivedFrom":subQ5}),-1.0]])]});}
            var Q62;
            Q62=makeQuery(id+"F0.imprint","IMPRINT",FACE,{"disambiguationData":[TD([[makeQuery(id+"F0.imprint","IMPRINT",EDGE,{"derivedFrom":sQuery(id+"F0.wireOp",EDGE,"E19.bottom")}),-1.0]])]});
            var Q63;
            {var subQ5=sQuery(id+"F0.wireOp",EDGE,"E11.0.7.0");Q63=makeQuery(id+"F0.imprint","IMPRINT",FACE,{"disambiguationData":[TD([[makeQuery(id+"F0.imprint","IMPRINT",EDGE,{"derivedFrom":subQ5}),-1.0]])]});}
            var Q64;
            {var subQ0=sQuery(id+"F0.wireOp",EDGE,"E11.9.5.0");var subQ1=sQuery(id+"F0.wireOp",EDGE,"E8.bottom");var subQ2=makeQuery(id+"F0.imprint","INTERSECT",VERTEX,{"derivedFrom":[subQ1,subQ0]});Q64=makeQuery(id+"F0.imprint","IMPRINT",FACE,{"disambiguationData":[TD([[makeQuery(id+"F0.imprint","IMPRINT",EDGE,{"disambiguationData":[TD([[subQ2,-1.0]])],"derivedFrom":subQ1}),-1.0]])]});}
            var Q65;
            {var subQ0=sQuery(id+"F0.wireOp",EDGE,"E18.bottom");var subQ1=sQuery(id+"F0.wireOp",EDGE,"E11.9.6.0");var subQ2=makeQuery(id+"F0.imprint","INTERSECT",VERTEX,{"derivedFrom":[subQ1,subQ0]});Q65=makeQuery(id+"F0.imprint","IMPRINT",FACE,{"disambiguationData":[TD([[makeQuery(id+"F0.imprint","IMPRINT",EDGE,{"disambiguationData":[TD([[subQ2,-1.0]])],"derivedFrom":subQ1}),1.0]])]});}
            var Q66;
            {var subQ5=sQuery(id+"F0.wireOp",EDGE,"E10.1.0.0");Q66=makeQuery(id+"F0.imprint","IMPRINT",FACE,{"disambiguationData":[TD([[makeQuery(id+"F0.imprint","IMPRINT",EDGE,{"derivedFrom":subQ5}),-1.0]])]});}
            var Q67;
            {var subQ0=sQuery(id+"F0.wireOp",EDGE,"E9.right");var subQ1=sQuery(id+"F0.wireOp",EDGE,"E8.bottom");var subQ2=makeQuery(id+"F0.imprint","INTERSECT",VERTEX,{"derivedFrom":[subQ1,subQ0]});Q67=makeQuery(id+"F0.imprint","IMPRINT",FACE,{"disambiguationData":[TD([[makeQuery(id+"F0.imprint","IMPRINT",EDGE,{"disambiguationData":[TD([[subQ2,-1.0]])],"derivedFrom":subQ1}),-1.0]])]});}
            var Q68;
            {var subQ5=sQuery(id+"F0.wireOp",EDGE,"E11.0.6.0");Q68=makeQuery(id+"F0.imprint","IMPRINT",FACE,{"disambiguationData":[TD([[makeQuery(id+"F0.imprint","IMPRINT",EDGE,{"derivedFrom":subQ5}),-1.0]])]});}
            var Q69;
            {var subQ0=sQuery(id+"F0.wireOp",EDGE,"E11.9.6.0");var subQ1=sQuery(id+"F0.wireOp",EDGE,"E8.top");var subQ2=makeQuery(id+"F0.imprint","INTERSECT",VERTEX,{"derivedFrom":[subQ1,subQ0]});Q69=makeQuery(id+"F0.imprint","IMPRINT",FACE,{"disambiguationData":[TD([[makeQuery(id+"F0.imprint","IMPRINT",EDGE,{"disambiguationData":[TD([[subQ2,-1.0]])],"derivedFrom":subQ1}),1.0]])]});}
            var Q70;
            {var subQ0=sQuery(id+"F0.wireOp",EDGE,"E11.9.6.0");var subQ5=sQuery(id+"F0.wireOp",EDGE,"E8.bottom");var subQ7=makeQuery(id+"F0.imprint","INTERSECT",VERTEX,{"derivedFrom":[subQ5,subQ0]});Q70=makeQuery(id+"F0.imprint","IMPRINT",FACE,{"disambiguationData":[TD([[makeQuery(id+"F0.imprint","IMPRINT",EDGE,{"disambiguationData":[TD([[subQ7,-1.0]])],"derivedFrom":subQ5}),1.0]])]});}
            var Q71;
            {var subQ0=sQuery(id+"F0.wireOp",EDGE,"E11.9.6.0");var subQ5=sQuery(id+"F0.wireOp",EDGE,"E8.top");var subQ7=makeQuery(id+"F0.imprint","INTERSECT",VERTEX,{"derivedFrom":[subQ5,subQ0]});Q71=makeQuery(id+"F0.imprint","IMPRINT",FACE,{"disambiguationData":[TD([[makeQuery(id+"F0.imprint","IMPRINT",EDGE,{"disambiguationData":[TD([[subQ7,-1.0]])],"derivedFrom":subQ5}),-1.0]])]});}
            var Q72;
            {var subQ0=sQuery(id+"F0.wireOp",EDGE,"E11.9.5.0");var subQ5=sQuery(id+"F0.wireOp",EDGE,"E8.bottom");var subQ6=makeQuery(id+"F0.imprint","INTERSECT",VERTEX,{"derivedFrom":[subQ5,subQ0]});Q72=makeQuery(id+"F0.imprint","IMPRINT",FACE,{"disambiguationData":[TD([[makeQuery(id+"F0.imprint","IMPRINT",EDGE,{"disambiguationData":[TD([[subQ6,-1.0]])],"derivedFrom":subQ5}),1.0]])]});}
            var Q73;
            {var subQ0=sQuery(id+"F0.wireOp",EDGE,"E11.9.5.0");var subQ5=sQuery(id+"F0.wireOp",EDGE,"E8.top");var subQ6=makeQuery(id+"F0.imprint","INTERSECT",VERTEX,{"derivedFrom":[subQ5,subQ0]});Q73=makeQuery(id+"F0.imprint","IMPRINT",FACE,{"disambiguationData":[TD([[makeQuery(id+"F0.imprint","IMPRINT",EDGE,{"disambiguationData":[TD([[subQ6,-1.0]])],"derivedFrom":subQ5}),-1.0]])]});}
            var Q74;
            {var subQ0=sQuery(id+"F0.wireOp",EDGE,"E11.9.4.0");var subQ5=sQuery(id+"F0.wireOp",EDGE,"E8.bottom");var subQ7=makeQuery(id+"F0.imprint","INTERSECT",VERTEX,{"derivedFrom":[subQ5,subQ0]});Q74=makeQuery(id+"F0.imprint","IMPRINT",FACE,{"disambiguationData":[TD([[makeQuery(id+"F0.imprint","IMPRINT",EDGE,{"disambiguationData":[TD([[subQ7,-1.0]])],"derivedFrom":subQ5}),1.0]])]});}
            var Q75;
            {var subQ0=sQuery(id+"F0.wireOp",EDGE,"E10.2.0.3");var subQ1=sQuery(id+"F0.wireOp",EDGE,"E8.top");var subQ2=makeQuery(id+"F0.imprint","INTERSECT",VERTEX,{"derivedFrom":[subQ1,subQ0]});Q75=makeQuery(id+"F0.imprint","IMPRINT",FACE,{"disambiguationData":[TD([[makeQuery(id+"F0.imprint","IMPRINT",EDGE,{"disambiguationData":[TD([[subQ2,-1.0]])],"derivedFrom":subQ1}),1.0]])]});}
            var Q76;
            {var subQ0=sQuery(id+"F0.wireOp",EDGE,"E11.9.3.0");var subQ5=sQuery(id+"F0.wireOp",EDGE,"E8.bottom");var subQ7=makeQuery(id+"F0.imprint","INTERSECT",VERTEX,{"derivedFrom":[subQ5,subQ0]});Q76=makeQuery(id+"F0.imprint","IMPRINT",FACE,{"disambiguationData":[TD([[makeQuery(id+"F0.imprint","IMPRINT",EDGE,{"disambiguationData":[TD([[subQ7,-1.0]])],"derivedFrom":subQ5}),1.0]])]});}
            var Q77;
            {var subQ0=sQuery(id+"F0.wireOp",EDGE,"E11.9.4.0");var subQ5=sQuery(id+"F0.wireOp",EDGE,"E8.top");var subQ6=makeQuery(id+"F0.imprint","INTERSECT",VERTEX,{"derivedFrom":[subQ5,subQ0]});Q77=makeQuery(id+"F0.imprint","IMPRINT",FACE,{"disambiguationData":[TD([[makeQuery(id+"F0.imprint","IMPRINT",EDGE,{"disambiguationData":[TD([[subQ6,-1.0]])],"derivedFrom":subQ5}),-1.0]])]});}
            var Q78;
            Q78=makeQuery(id+"F0.imprint","IMPRINT",FACE,{"disambiguationData":[TD([[makeQuery(id+"F0.imprint","IMPRINT",EDGE,{"derivedFrom":sQuery(id+"F0.wireOp",EDGE,"E3")}),1.0]])]});
            var Q79;
            Q79=makeQuery(id+"F0.imprint","IMPRINT",FACE,{"disambiguationData":[TD([[makeQuery(id+"F0.imprint","IMPRINT",EDGE,{"derivedFrom":sQuery(id+"F0.wireOp",EDGE,"E2")}),1.0]])]});
            var Q80;
            Q80=makeQuery(id+"F0.imprint","IMPRINT",FACE,{"disambiguationData":[TD([[makeQuery(id+"F0.imprint","IMPRINT",EDGE,{"derivedFrom":sQuery(id+"F0.wireOp",EDGE,"E1")}),1.0]])]});
            var Q81;
            {var subQ0=sQuery(id+"F0.wireOp",EDGE,"E11.9.3.0");var subQ5=sQuery(id+"F0.wireOp",EDGE,"E8.top");var subQ6=makeQuery(id+"F0.imprint","INTERSECT",VERTEX,{"derivedFrom":[subQ5,subQ0]});Q81=makeQuery(id+"F0.imprint","IMPRINT",FACE,{"disambiguationData":[TD([[makeQuery(id+"F0.imprint","IMPRINT",EDGE,{"disambiguationData":[TD([[subQ6,-1.0]])],"derivedFrom":subQ5}),-1.0]])]});}
            var Q82;
            {var subQ0=sQuery(id+"F0.wireOp",EDGE,"E10.2.0.3");var subQ5=sQuery(id+"F0.wireOp",EDGE,"E8.bottom");var subQ6=makeQuery(id+"F0.imprint","INTERSECT",VERTEX,{"derivedFrom":[subQ5,subQ0]});Q82=makeQuery(id+"F0.imprint","IMPRINT",FACE,{"disambiguationData":[TD([[makeQuery(id+"F0.imprint","IMPRINT",EDGE,{"disambiguationData":[TD([[subQ6,-1.0]])],"derivedFrom":subQ5}),1.0]])]});}
            var Q83;
            {var subQ0=sQuery(id+"F0.wireOp",EDGE,"E10.1.0.3");var subQ5=sQuery(id+"F0.wireOp",EDGE,"E8.bottom");var subQ6=makeQuery(id+"F0.imprint","INTERSECT",VERTEX,{"derivedFrom":[subQ5,subQ0]});Q83=makeQuery(id+"F0.imprint","IMPRINT",FACE,{"disambiguationData":[TD([[makeQuery(id+"F0.imprint","IMPRINT",EDGE,{"disambiguationData":[TD([[subQ6,-1.0]])],"derivedFrom":subQ5}),1.0]])]});}
            var Q84;
            {var subQ0=sQuery(id+"F0.wireOp",EDGE,"E10.2.0.3");var subQ5=sQuery(id+"F0.wireOp",EDGE,"E8.top");var subQ6=makeQuery(id+"F0.imprint","INTERSECT",VERTEX,{"derivedFrom":[subQ5,subQ0]});Q84=makeQuery(id+"F0.imprint","IMPRINT",FACE,{"disambiguationData":[TD([[makeQuery(id+"F0.imprint","IMPRINT",EDGE,{"disambiguationData":[TD([[subQ6,-1.0]])],"derivedFrom":subQ5}),-1.0]])]});}
            var Q85;
            {var subQ0=sQuery(id+"F0.wireOp",EDGE,"E10.1.0.3");var subQ5=sQuery(id+"F0.wireOp",EDGE,"E8.top");var subQ6=makeQuery(id+"F0.imprint","INTERSECT",VERTEX,{"derivedFrom":[subQ5,subQ0]});Q85=makeQuery(id+"F0.imprint","IMPRINT",FACE,{"disambiguationData":[TD([[makeQuery(id+"F0.imprint","IMPRINT",EDGE,{"disambiguationData":[TD([[subQ6,-1.0]])],"derivedFrom":subQ5}),-1.0]])]});}
            var Q86;
            {var subQ0=sQuery(id+"F0.wireOp",EDGE,"E11.9.4.0");var subQ1=sQuery(id+"F0.wireOp",EDGE,"E8.bottom");var subQ2=makeQuery(id+"F0.imprint","INTERSECT",VERTEX,{"derivedFrom":[subQ1,subQ0]});Q86=makeQuery(id+"F0.imprint","IMPRINT",FACE,{"disambiguationData":[TD([[makeQuery(id+"F0.imprint","IMPRINT",EDGE,{"disambiguationData":[TD([[subQ2,-1.0]])],"derivedFrom":subQ1}),-1.0]])]});}
            var Q87;
            {var subQ0=sQuery(id+"F0.wireOp",EDGE,"E10.2.0.3");var subQ1=sQuery(id+"F0.wireOp",EDGE,"E8.bottom");var subQ2=makeQuery(id+"F0.imprint","INTERSECT",VERTEX,{"derivedFrom":[subQ1,subQ0]});Q87=makeQuery(id+"F0.imprint","IMPRINT",FACE,{"disambiguationData":[TD([[makeQuery(id+"F0.imprint","IMPRINT",EDGE,{"disambiguationData":[TD([[subQ2,-1.0]])],"derivedFrom":subQ1}),-1.0]])]});}
            var Q88;
            {var subQ0=sQuery(id+"F0.wireOp",EDGE,"E9.right");var subQ5=sQuery(id+"F0.wireOp",EDGE,"E8.top");var subQ6=makeQuery(id+"F0.imprint","INTERSECT",VERTEX,{"derivedFrom":[subQ5,subQ0]});Q88=makeQuery(id+"F0.imprint","IMPRINT",FACE,{"disambiguationData":[TD([[makeQuery(id+"F0.imprint","IMPRINT",EDGE,{"disambiguationData":[TD([[subQ6,-1.0]])],"derivedFrom":subQ5}),-1.0]])]});}
            var Q89;
            {var subQ0=sQuery(id+"F0.wireOp",EDGE,"E10.1.0.3");var subQ1=sQuery(id+"F0.wireOp",EDGE,"E8.bottom");var subQ2=makeQuery(id+"F0.imprint","INTERSECT",VERTEX,{"derivedFrom":[subQ1,subQ0]});Q89=makeQuery(id+"F0.imprint","IMPRINT",FACE,{"disambiguationData":[TD([[makeQuery(id+"F0.imprint","IMPRINT",EDGE,{"disambiguationData":[TD([[subQ2,-1.0]])],"derivedFrom":subQ1}),-1.0]])]});}
            var Q90;
            {var subQ0=sQuery(id+"F0.wireOp",EDGE,"E11.9.4.0");var subQ1=sQuery(id+"F0.wireOp",EDGE,"E8.top");var subQ2=makeQuery(id+"F0.imprint","INTERSECT",VERTEX,{"derivedFrom":[subQ1,subQ0]});Q90=makeQuery(id+"F0.imprint","IMPRINT",FACE,{"disambiguationData":[TD([[makeQuery(id+"F0.imprint","IMPRINT",EDGE,{"disambiguationData":[TD([[subQ2,-1.0]])],"derivedFrom":subQ1}),1.0]])]});}
            var Q91;
            {var subQ0=sQuery(id+"F0.wireOp",EDGE,"E9.right");var subQ5=sQuery(id+"F0.wireOp",EDGE,"E8.bottom");var subQ6=makeQuery(id+"F0.imprint","INTERSECT",VERTEX,{"derivedFrom":[subQ5,subQ0]});Q91=makeQuery(id+"F0.imprint","IMPRINT",FACE,{"disambiguationData":[TD([[makeQuery(id+"F0.imprint","IMPRINT",EDGE,{"disambiguationData":[TD([[subQ6,-1.0]])],"derivedFrom":subQ5}),1.0]])]});}
            var Q92;
            {var subQ5=sQuery(id+"F0.wireOp",EDGE,"E9.top");Q92=makeQuery(id+"F0.imprint","IMPRINT",FACE,{"disambiguationData":[TD([[makeQuery(id+"F0.imprint","IMPRINT",EDGE,{"derivedFrom":subQ5}),1.0]])]});}
            var Q93;
            Q93=makeQuery(id+"F0.imprint","IMPRINT",FACE,{"disambiguationData":[TD([[makeQuery(id+"F0.imprint","IMPRINT",EDGE,{"derivedFrom":sQuery(id+"F0.wireOp",EDGE,"IHaIXLzq-n4hj-2AC6-2CWR-DmoSdEm5e3l4.bottom")}),-1.0]])]});
            var Q94;
            {var subQ34=sQuery(id+"F0.wireOp",EDGE,"E9.bottom");Q94=makeQuery(id+"F0.imprint","IMPRINT",FACE,{"disambiguationData":[TD([[makeQuery(id+"F0.imprint","IMPRINT",EDGE,{"derivedFrom":subQ34}),1.0]])]});}
            var Q95;
            {var subQ0=sQuery(id+"F0.wireOp",EDGE,"E7.left");Q95=makeQuery(id+"F0.imprint","IMPRINT",FACE,{"disambiguationData":[TD([[makeQuery(id+"F0.imprint","IMPRINT",EDGE,{"derivedFrom":subQ0}),1.0]])]});}
            var Q96;
            {var subQ0=sQuery(id+"F0.wireOp",EDGE,"E9.left");var subQ1=sQuery(id+"F0.wireOp",EDGE,"E8.top");var subQ2=makeQuery(id+"F0.imprint","INTERSECT",VERTEX,{"derivedFrom":[subQ1,subQ0]});Q96=makeQuery(id+"F0.imprint","IMPRINT",FACE,{"disambiguationData":[TD([[makeQuery(id+"F0.imprint","IMPRINT",EDGE,{"disambiguationData":[TD([[subQ2,-1.0]])],"derivedFrom":subQ1}),1.0]])]});}
            var Q97;
            {var subQ5=sQuery(id+"F0.wireOp",EDGE,"E18.left");Q97=makeQuery(id+"F0.imprint","IMPRINT",FACE,{"disambiguationData":[TD([[makeQuery(id+"F0.imprint","IMPRINT",EDGE,{"derivedFrom":subQ5}),1.0]])]});}
            var Q98;
            {var subQ0=sQuery(id+"F0.wireOp",EDGE,"E8.left");Q98=makeQuery(id+"F0.imprint","IMPRINT",FACE,{"disambiguationData":[TD([[makeQuery(id+"F0.imprint","IMPRINT",EDGE,{"derivedFrom":subQ0}),1.0]])]});}
            var Q99;
            Q99=makeQuery(id+"F0.imprint","IMPRINT",FACE,{"disambiguationData":[TD([[makeQuery(id+"F0.imprint","IMPRINT",EDGE,{"derivedFrom":sQuery(id+"F0.wireOp",EDGE,"E16")}),-1.0]])]});
            var Q100;
            Q100=makeQuery(id+"F0.imprint","IMPRINT",FACE,{"disambiguationData":[TD([[makeQuery(id+"F0.imprint","IMPRINT",EDGE,{"derivedFrom":sQuery(id+"F0.wireOp",EDGE,"E17")}),-1.0]])]});
            var Q101;
            Q101=makeQuery(id+"F0.imprint","IMPRINT",FACE,{"disambiguationData":[TD([[makeQuery(id+"F0.imprint","IMPRINT",EDGE,{"derivedFrom":sQuery(id+"F0.wireOp",EDGE,"E16")}),1.0]])]});
            var Q102;
            Q102=makeQuery(id+"F0.imprint","IMPRINT",FACE,{"disambiguationData":[TD([[makeQuery(id+"F0.imprint","IMPRINT",EDGE,{"derivedFrom":sQuery(id+"F0.wireOp",EDGE,"E17")}),1.0]])]});
            var Q103;
            {var subQ0=sQuery(id+"F0.wireOp",EDGE,"E26");Q103=makeQuery(id+"F0.imprint","IMPRINT",FACE,{"disambiguationData":[TD([[makeQuery(id+"F0.imprint","IMPRINT",EDGE,{"derivedFrom":subQ0}),1.0]])]});}
            var Q104;
            {var subQ0=sQuery(id+"F0.wireOp",EDGE,"E27");Q104=makeQuery(id+"F0.imprint","IMPRINT",FACE,{"disambiguationData":[TD([[makeQuery(id+"F0.imprint","IMPRINT",EDGE,{"derivedFrom":subQ0}),-1.0]])]});}
            var Q105;
            {var subQ1=sQuery(id+"F0.wireOp",EDGE,"E20.right");Q105=makeQuery(id+"F0.imprint","IMPRINT",FACE,{"disambiguationData":[TD([[makeQuery(id+"F0.imprint","IMPRINT",EDGE,{"derivedFrom":subQ1}),-1.0]])]});}
            var Q106;
            Q106=makeQuery(id+"F0.imprint","IMPRINT",FACE,{"disambiguationData":[TD([[makeQuery(id+"F0.imprint","IMPRINT",EDGE,{"derivedFrom":sQuery(id+"F0.wireOp",EDGE,"E30")}),1.0]])]});
            var Q107;
            {var subQ0=sQuery(id+"F0.wireOp",EDGE,"E21.right");Q107=makeQuery(id+"F0.imprint","IMPRINT",FACE,{"disambiguationData":[TD([[makeQuery(id+"F0.imprint","IMPRINT",EDGE,{"derivedFrom":subQ0}),1.0]])]});}
            var Q108;
            Q108=makeQuery(id+"F0.imprint","IMPRINT",FACE,{"disambiguationData":[TD([[makeQuery(id+"F0.imprint","IMPRINT",EDGE,{"derivedFrom":sQuery(id+"F0.wireOp",EDGE,"E31")}),1.0]])]});
            extrude(context, id + "F1", {"entities" : qUnion([Q0, Q1, Q2, Q3, Q4, Q5, Q6, Q7, Q8, Q9, Q10, Q11, Q12, Q13, Q14, Q15, Q16, Q17, Q18, Q19, Q20, Q21, Q22, Q23, Q24, Q25, Q26, Q27, Q28, Q29, Q30, Q31, Q32, Q33, Q34, Q35, Q36, Q37, Q38, Q39, Q40, Q41, Q42, Q43, Q44, Q45, Q46, Q47, Q48, Q49, Q50, Q51, Q52, Q53, Q54, Q55, Q56, Q57, Q58, Q59, Q60, Q61, Q62, Q63, Q64, Q65, Q66, Q67, Q68, Q69, Q70, Q71, Q72, Q73, Q74, Q75, Q76, Q77, Q78, Q79, Q80, Q81, Q82, Q83, Q84, Q85, Q86, Q87, Q88, Q89, Q90, Q91, Q92, Q93, Q94, Q95, Q96, Q97, Q98, Q99, Q100, Q101, Q102, Q103, Q104, Q105, Q106, Q107, Q108]), "oppositeDirection" : true, "depth" : 5.08 * mm});
        }
        {
            var Q0;
            {var subQ23=sQuery(id+"F0.wireOp",EDGE,"E4.top");Q0=makeQuery(id+"F0.imprint","IMPRINT",FACE,{"disambiguationData":[TD([[makeQuery(id+"F0.imprint","IMPRINT",EDGE,{"derivedFrom":subQ23}),1.0]])]});}
            var Q1;
            {var subQ0=sQuery(id+"F0.wireOp",EDGE,"E4.top");Q1=makeQuery(id+"F0.imprint","IMPRINT",FACE,{"disambiguationData":[TD([[makeQuery(id+"F0.imprint","IMPRINT",EDGE,{"derivedFrom":subQ0}),-1.0]])]});}
            var Q2;
            {var subQ0=sQuery(id+"F0.wireOp",EDGE,"E5.top");Q2=makeQuery(id+"F0.imprint","IMPRINT",FACE,{"disambiguationData":[TD([[makeQuery(id+"F0.imprint","IMPRINT",EDGE,{"derivedFrom":subQ0}),-1.0]])]});}
            var Q3;
            {var subQ34=sQuery(id+"F0.wireOp",EDGE,"E9.bottom");Q3=makeQuery(id+"F0.imprint","IMPRINT",FACE,{"disambiguationData":[TD([[makeQuery(id+"F0.imprint","IMPRINT",EDGE,{"derivedFrom":subQ34}),1.0]])]});}
            extrude(context, id + "F2", {"entities" : qUnion([Q0, Q1, Q2, Q3]), "operationType" : NewBodyOperationType.REMOVE, "oppositeDirection" : true, "depth" : 3.8 * mm});
        }
        {
            var Q0;
            Q0=makeQuery(id+"F0.imprint","IMPRINT",FACE,{"disambiguationData":[TD([[makeQuery(id+"F0.imprint","IMPRINT",EDGE,{"derivedFrom":sQuery(id+"F0.wireOp",EDGE,"E1")}),-1.0]])]});
            var Q1;
            Q1=makeQuery(id+"F0.imprint","IMPRINT",FACE,{"disambiguationData":[TD([[makeQuery(id+"F0.imprint","IMPRINT",EDGE,{"derivedFrom":sQuery(id+"F0.wireOp",EDGE,"E3")}),-1.0]])]});
            var Q2;
            Q2=makeQuery(id+"F0.imprint","IMPRINT",FACE,{"disambiguationData":[TD([[makeQuery(id+"F0.imprint","IMPRINT",EDGE,{"derivedFrom":sQuery(id+"F0.wireOp",EDGE,"E2")}),-1.0]])]});
            var Q3;
            Q3=makeQuery(id+"F0.imprint","IMPRINT",FACE,{"disambiguationData":[TD([[makeQuery(id+"F0.imprint","IMPRINT",EDGE,{"derivedFrom":sQuery(id+"F0.wireOp",EDGE,"E15.bottom")}),1.0]])]});
            extrude(context, id + "F3", {"entities" : qUnion([Q0, Q1, Q2, Q3]), "operationType" : NewBodyOperationType.REMOVE, "oppositeDirection" : true, "depth" : 1.52 * mm});
        }
        {
            var Q0;
            Q0=makeQuery(id+"F0.imprint","IMPRINT",FACE,{"disambiguationData":[TD([[makeQuery(id+"F0.imprint","IMPRINT",EDGE,{"derivedFrom":sQuery(id+"F0.wireOp",EDGE,"E1")}),1.0]])]});
            var Q1;
            Q1=makeQuery(id+"F0.imprint","IMPRINT",FACE,{"disambiguationData":[TD([[makeQuery(id+"F0.imprint","IMPRINT",EDGE,{"derivedFrom":sQuery(id+"F0.wireOp",EDGE,"E2")}),1.0]])]});
            var Q2;
            Q2=makeQuery(id+"F0.imprint","IMPRINT",FACE,{"disambiguationData":[TD([[makeQuery(id+"F0.imprint","IMPRINT",EDGE,{"derivedFrom":sQuery(id+"F0.wireOp",EDGE,"E3")}),1.0]])]});
            var Q3;
            {var subQ5=sQuery(id+"F0.wireOp",EDGE,"E19.left");Q3=makeQuery(id+"F0.imprint","IMPRINT",FACE,{"disambiguationData":[TD([[makeQuery(id+"F0.imprint","IMPRINT",EDGE,{"derivedFrom":subQ5}),-1.0]])]});}
            var Q4;
            Q4=makeQuery(id+"F0.imprint","IMPRINT",FACE,{"disambiguationData":[TD([[makeQuery(id+"F0.imprint","IMPRINT",EDGE,{"derivedFrom":sQuery(id+"F0.wireOp",EDGE,"E19.bottom")}),-1.0]])]});
            var Q5;
            {var subQ5=sQuery(id+"F0.wireOp",EDGE,"E19.right");Q5=makeQuery(id+"F0.imprint","IMPRINT",FACE,{"disambiguationData":[TD([[makeQuery(id+"F0.imprint","IMPRINT",EDGE,{"derivedFrom":subQ5}),1.0]])]});}
            extrude(context, id + "F4", {"entities" : qUnion([Q0, Q1, Q2, Q3, Q4, Q5]), "operationType" : NewBodyOperationType.ADD, "depth" : 2.54 * mm});
        }
        {
            var Q0;
            {var subQ0=sQuery(id+"F0.wireOp",EDGE,"E7.left");Q0=makeQuery(id+"F0.imprint","IMPRINT",FACE,{"disambiguationData":[TD([[makeQuery(id+"F0.imprint","IMPRINT",EDGE,{"derivedFrom":subQ0}),1.0]])]});}
            var Q1;
            {var subQ0=sQuery(id+"F0.wireOp",EDGE,"E9.right");var subQ5=sQuery(id+"F0.wireOp",EDGE,"E8.top");var subQ6=makeQuery(id+"F0.imprint","INTERSECT",VERTEX,{"derivedFrom":[subQ5,subQ0]});Q1=makeQuery(id+"F0.imprint","IMPRINT",FACE,{"disambiguationData":[TD([[makeQuery(id+"F0.imprint","IMPRINT",EDGE,{"disambiguationData":[TD([[subQ6,-1.0]])],"derivedFrom":subQ5}),-1.0]])]});}
            var Q2;
            {var subQ0=sQuery(id+"F0.wireOp",EDGE,"E9.right");var subQ1=sQuery(id+"F0.wireOp",EDGE,"E8.top");var subQ2=makeQuery(id+"F0.imprint","INTERSECT",VERTEX,{"derivedFrom":[subQ1,subQ0]});Q2=makeQuery(id+"F0.imprint","IMPRINT",FACE,{"disambiguationData":[TD([[makeQuery(id+"F0.imprint","IMPRINT",EDGE,{"disambiguationData":[TD([[subQ2,-1.0]])],"derivedFrom":subQ1}),1.0]])]});}
            var Q3;
            {var subQ0=sQuery(id+"F0.wireOp",EDGE,"E9.right");var subQ1=sQuery(id+"F0.wireOp",EDGE,"E8.bottom");var subQ2=makeQuery(id+"F0.imprint","INTERSECT",VERTEX,{"derivedFrom":[subQ1,subQ0]});Q3=makeQuery(id+"F0.imprint","IMPRINT",FACE,{"disambiguationData":[TD([[makeQuery(id+"F0.imprint","IMPRINT",EDGE,{"disambiguationData":[TD([[subQ2,-1.0]])],"derivedFrom":subQ1}),-1.0]])]});}
            var Q4;
            {var subQ0=sQuery(id+"F0.wireOp",EDGE,"E9.right");var subQ5=sQuery(id+"F0.wireOp",EDGE,"E8.bottom");var subQ6=makeQuery(id+"F0.imprint","INTERSECT",VERTEX,{"derivedFrom":[subQ5,subQ0]});Q4=makeQuery(id+"F0.imprint","IMPRINT",FACE,{"disambiguationData":[TD([[makeQuery(id+"F0.imprint","IMPRINT",EDGE,{"disambiguationData":[TD([[subQ6,-1.0]])],"derivedFrom":subQ5}),1.0]])]});}
            var Q5;
            {var subQ0=sQuery(id+"F0.wireOp",EDGE,"E10.1.0.3");var subQ5=sQuery(id+"F0.wireOp",EDGE,"E8.bottom");var subQ6=makeQuery(id+"F0.imprint","INTERSECT",VERTEX,{"derivedFrom":[subQ5,subQ0]});Q5=makeQuery(id+"F0.imprint","IMPRINT",FACE,{"disambiguationData":[TD([[makeQuery(id+"F0.imprint","IMPRINT",EDGE,{"disambiguationData":[TD([[subQ6,-1.0]])],"derivedFrom":subQ5}),1.0]])]});}
            var Q6;
            {var subQ0=sQuery(id+"F0.wireOp",EDGE,"E10.2.0.3");var subQ5=sQuery(id+"F0.wireOp",EDGE,"E8.bottom");var subQ6=makeQuery(id+"F0.imprint","INTERSECT",VERTEX,{"derivedFrom":[subQ5,subQ0]});Q6=makeQuery(id+"F0.imprint","IMPRINT",FACE,{"disambiguationData":[TD([[makeQuery(id+"F0.imprint","IMPRINT",EDGE,{"disambiguationData":[TD([[subQ6,-1.0]])],"derivedFrom":subQ5}),1.0]])]});}
            var Q7;
            {var subQ0=sQuery(id+"F0.wireOp",EDGE,"E11.9.3.0");var subQ5=sQuery(id+"F0.wireOp",EDGE,"E8.bottom");var subQ7=makeQuery(id+"F0.imprint","INTERSECT",VERTEX,{"derivedFrom":[subQ5,subQ0]});Q7=makeQuery(id+"F0.imprint","IMPRINT",FACE,{"disambiguationData":[TD([[makeQuery(id+"F0.imprint","IMPRINT",EDGE,{"disambiguationData":[TD([[subQ7,-1.0]])],"derivedFrom":subQ5}),1.0]])]});}
            var Q8;
            {var subQ0=sQuery(id+"F0.wireOp",EDGE,"E11.9.4.0");var subQ5=sQuery(id+"F0.wireOp",EDGE,"E8.bottom");var subQ7=makeQuery(id+"F0.imprint","INTERSECT",VERTEX,{"derivedFrom":[subQ5,subQ0]});Q8=makeQuery(id+"F0.imprint","IMPRINT",FACE,{"disambiguationData":[TD([[makeQuery(id+"F0.imprint","IMPRINT",EDGE,{"disambiguationData":[TD([[subQ7,-1.0]])],"derivedFrom":subQ5}),1.0]])]});}
            var Q9;
            {var subQ0=sQuery(id+"F0.wireOp",EDGE,"E11.9.5.0");var subQ5=sQuery(id+"F0.wireOp",EDGE,"E8.bottom");var subQ6=makeQuery(id+"F0.imprint","INTERSECT",VERTEX,{"derivedFrom":[subQ5,subQ0]});Q9=makeQuery(id+"F0.imprint","IMPRINT",FACE,{"disambiguationData":[TD([[makeQuery(id+"F0.imprint","IMPRINT",EDGE,{"disambiguationData":[TD([[subQ6,-1.0]])],"derivedFrom":subQ5}),1.0]])]});}
            var Q10;
            {var subQ0=sQuery(id+"F0.wireOp",EDGE,"E11.9.5.0");var subQ1=sQuery(id+"F0.wireOp",EDGE,"E8.bottom");var subQ2=makeQuery(id+"F0.imprint","INTERSECT",VERTEX,{"derivedFrom":[subQ1,subQ0]});Q10=makeQuery(id+"F0.imprint","IMPRINT",FACE,{"disambiguationData":[TD([[makeQuery(id+"F0.imprint","IMPRINT",EDGE,{"disambiguationData":[TD([[subQ2,-1.0]])],"derivedFrom":subQ1}),-1.0]])]});}
            var Q11;
            {var subQ0=sQuery(id+"F0.wireOp",EDGE,"E11.9.4.0");var subQ1=sQuery(id+"F0.wireOp",EDGE,"E8.bottom");var subQ2=makeQuery(id+"F0.imprint","INTERSECT",VERTEX,{"derivedFrom":[subQ1,subQ0]});Q11=makeQuery(id+"F0.imprint","IMPRINT",FACE,{"disambiguationData":[TD([[makeQuery(id+"F0.imprint","IMPRINT",EDGE,{"disambiguationData":[TD([[subQ2,-1.0]])],"derivedFrom":subQ1}),-1.0]])]});}
            var Q12;
            {var subQ0=sQuery(id+"F0.wireOp",EDGE,"E11.9.3.0");var subQ1=sQuery(id+"F0.wireOp",EDGE,"E8.bottom");var subQ2=makeQuery(id+"F0.imprint","INTERSECT",VERTEX,{"derivedFrom":[subQ1,subQ0]});Q12=makeQuery(id+"F0.imprint","IMPRINT",FACE,{"disambiguationData":[TD([[makeQuery(id+"F0.imprint","IMPRINT",EDGE,{"disambiguationData":[TD([[subQ2,-1.0]])],"derivedFrom":subQ1}),-1.0]])]});}
            var Q13;
            {var subQ0=sQuery(id+"F0.wireOp",EDGE,"E10.2.0.3");var subQ1=sQuery(id+"F0.wireOp",EDGE,"E8.bottom");var subQ2=makeQuery(id+"F0.imprint","INTERSECT",VERTEX,{"derivedFrom":[subQ1,subQ0]});Q13=makeQuery(id+"F0.imprint","IMPRINT",FACE,{"disambiguationData":[TD([[makeQuery(id+"F0.imprint","IMPRINT",EDGE,{"disambiguationData":[TD([[subQ2,-1.0]])],"derivedFrom":subQ1}),-1.0]])]});}
            var Q14;
            {var subQ0=sQuery(id+"F0.wireOp",EDGE,"E10.1.0.3");var subQ1=sQuery(id+"F0.wireOp",EDGE,"E8.bottom");var subQ2=makeQuery(id+"F0.imprint","INTERSECT",VERTEX,{"derivedFrom":[subQ1,subQ0]});Q14=makeQuery(id+"F0.imprint","IMPRINT",FACE,{"disambiguationData":[TD([[makeQuery(id+"F0.imprint","IMPRINT",EDGE,{"disambiguationData":[TD([[subQ2,-1.0]])],"derivedFrom":subQ1}),-1.0]])]});}
            var Q15;
            {var subQ0=sQuery(id+"F0.wireOp",EDGE,"E10.1.0.3");var subQ1=sQuery(id+"F0.wireOp",EDGE,"E8.top");var subQ2=makeQuery(id+"F0.imprint","INTERSECT",VERTEX,{"derivedFrom":[subQ1,subQ0]});Q15=makeQuery(id+"F0.imprint","IMPRINT",FACE,{"disambiguationData":[TD([[makeQuery(id+"F0.imprint","IMPRINT",EDGE,{"disambiguationData":[TD([[subQ2,-1.0]])],"derivedFrom":subQ1}),1.0]])]});}
            var Q16;
            {var subQ0=sQuery(id+"F0.wireOp",EDGE,"E10.2.0.3");var subQ1=sQuery(id+"F0.wireOp",EDGE,"E8.top");var subQ2=makeQuery(id+"F0.imprint","INTERSECT",VERTEX,{"derivedFrom":[subQ1,subQ0]});Q16=makeQuery(id+"F0.imprint","IMPRINT",FACE,{"disambiguationData":[TD([[makeQuery(id+"F0.imprint","IMPRINT",EDGE,{"disambiguationData":[TD([[subQ2,-1.0]])],"derivedFrom":subQ1}),1.0]])]});}
            var Q17;
            {var subQ0=sQuery(id+"F0.wireOp",EDGE,"E11.9.3.0");var subQ1=sQuery(id+"F0.wireOp",EDGE,"E8.top");var subQ2=makeQuery(id+"F0.imprint","INTERSECT",VERTEX,{"derivedFrom":[subQ1,subQ0]});Q17=makeQuery(id+"F0.imprint","IMPRINT",FACE,{"disambiguationData":[TD([[makeQuery(id+"F0.imprint","IMPRINT",EDGE,{"disambiguationData":[TD([[subQ2,-1.0]])],"derivedFrom":subQ1}),1.0]])]});}
            var Q18;
            {var subQ0=sQuery(id+"F0.wireOp",EDGE,"E11.9.4.0");var subQ1=sQuery(id+"F0.wireOp",EDGE,"E8.top");var subQ2=makeQuery(id+"F0.imprint","INTERSECT",VERTEX,{"derivedFrom":[subQ1,subQ0]});Q18=makeQuery(id+"F0.imprint","IMPRINT",FACE,{"disambiguationData":[TD([[makeQuery(id+"F0.imprint","IMPRINT",EDGE,{"disambiguationData":[TD([[subQ2,-1.0]])],"derivedFrom":subQ1}),1.0]])]});}
            var Q19;
            {var subQ0=sQuery(id+"F0.wireOp",EDGE,"E11.9.5.0");var subQ1=sQuery(id+"F0.wireOp",EDGE,"E8.top");var subQ2=makeQuery(id+"F0.imprint","INTERSECT",VERTEX,{"derivedFrom":[subQ1,subQ0]});Q19=makeQuery(id+"F0.imprint","IMPRINT",FACE,{"disambiguationData":[TD([[makeQuery(id+"F0.imprint","IMPRINT",EDGE,{"disambiguationData":[TD([[subQ2,-1.0]])],"derivedFrom":subQ1}),1.0]])]});}
            var Q20;
            {var subQ0=sQuery(id+"F0.wireOp",EDGE,"E11.9.4.0");var subQ5=sQuery(id+"F0.wireOp",EDGE,"E8.top");var subQ6=makeQuery(id+"F0.imprint","INTERSECT",VERTEX,{"derivedFrom":[subQ5,subQ0]});Q20=makeQuery(id+"F0.imprint","IMPRINT",FACE,{"disambiguationData":[TD([[makeQuery(id+"F0.imprint","IMPRINT",EDGE,{"disambiguationData":[TD([[subQ6,-1.0]])],"derivedFrom":subQ5}),-1.0]])]});}
            var Q21;
            {var subQ0=sQuery(id+"F0.wireOp",EDGE,"E11.9.3.0");var subQ5=sQuery(id+"F0.wireOp",EDGE,"E8.top");var subQ6=makeQuery(id+"F0.imprint","INTERSECT",VERTEX,{"derivedFrom":[subQ5,subQ0]});Q21=makeQuery(id+"F0.imprint","IMPRINT",FACE,{"disambiguationData":[TD([[makeQuery(id+"F0.imprint","IMPRINT",EDGE,{"disambiguationData":[TD([[subQ6,-1.0]])],"derivedFrom":subQ5}),-1.0]])]});}
            var Q22;
            {var subQ0=sQuery(id+"F0.wireOp",EDGE,"E10.2.0.3");var subQ5=sQuery(id+"F0.wireOp",EDGE,"E8.top");var subQ6=makeQuery(id+"F0.imprint","INTERSECT",VERTEX,{"derivedFrom":[subQ5,subQ0]});Q22=makeQuery(id+"F0.imprint","IMPRINT",FACE,{"disambiguationData":[TD([[makeQuery(id+"F0.imprint","IMPRINT",EDGE,{"disambiguationData":[TD([[subQ6,-1.0]])],"derivedFrom":subQ5}),-1.0]])]});}
            var Q23;
            {var subQ0=sQuery(id+"F0.wireOp",EDGE,"E10.1.0.3");var subQ5=sQuery(id+"F0.wireOp",EDGE,"E8.top");var subQ6=makeQuery(id+"F0.imprint","INTERSECT",VERTEX,{"derivedFrom":[subQ5,subQ0]});Q23=makeQuery(id+"F0.imprint","IMPRINT",FACE,{"disambiguationData":[TD([[makeQuery(id+"F0.imprint","IMPRINT",EDGE,{"disambiguationData":[TD([[subQ6,-1.0]])],"derivedFrom":subQ5}),-1.0]])]});}
            var Q24;
            {var subQ0=sQuery(id+"F0.wireOp",EDGE,"E11.9.5.0");var subQ5=sQuery(id+"F0.wireOp",EDGE,"E8.top");var subQ6=makeQuery(id+"F0.imprint","INTERSECT",VERTEX,{"derivedFrom":[subQ5,subQ0]});Q24=makeQuery(id+"F0.imprint","IMPRINT",FACE,{"disambiguationData":[TD([[makeQuery(id+"F0.imprint","IMPRINT",EDGE,{"disambiguationData":[TD([[subQ6,-1.0]])],"derivedFrom":subQ5}),-1.0]])]});}
            var Q25;
            {var subQ0=sQuery(id+"F0.wireOp",EDGE,"E11.9.6.0");var subQ5=sQuery(id+"F0.wireOp",EDGE,"E8.top");var subQ7=makeQuery(id+"F0.imprint","INTERSECT",VERTEX,{"derivedFrom":[subQ5,subQ0]});Q25=makeQuery(id+"F0.imprint","IMPRINT",FACE,{"disambiguationData":[TD([[makeQuery(id+"F0.imprint","IMPRINT",EDGE,{"disambiguationData":[TD([[subQ7,-1.0]])],"derivedFrom":subQ5}),-1.0]])]});}
            var Q26;
            {var subQ0=sQuery(id+"F0.wireOp",EDGE,"E11.9.6.0");var subQ1=sQuery(id+"F0.wireOp",EDGE,"E8.top");var subQ2=makeQuery(id+"F0.imprint","INTERSECT",VERTEX,{"derivedFrom":[subQ1,subQ0]});Q26=makeQuery(id+"F0.imprint","IMPRINT",FACE,{"disambiguationData":[TD([[makeQuery(id+"F0.imprint","IMPRINT",EDGE,{"disambiguationData":[TD([[subQ2,-1.0]])],"derivedFrom":subQ1}),1.0]])]});}
            var Q27;
            {var subQ0=sQuery(id+"F0.wireOp",EDGE,"E11.9.6.0");var subQ5=sQuery(id+"F0.wireOp",EDGE,"E8.bottom");var subQ7=makeQuery(id+"F0.imprint","INTERSECT",VERTEX,{"derivedFrom":[subQ5,subQ0]});Q27=makeQuery(id+"F0.imprint","IMPRINT",FACE,{"disambiguationData":[TD([[makeQuery(id+"F0.imprint","IMPRINT",EDGE,{"disambiguationData":[TD([[subQ7,-1.0]])],"derivedFrom":subQ5}),1.0]])]});}
            var Q28;
            {var subQ0=sQuery(id+"F0.wireOp",EDGE,"E11.9.6.0");var subQ1=sQuery(id+"F0.wireOp",EDGE,"E8.bottom");var subQ2=makeQuery(id+"F0.imprint","INTERSECT",VERTEX,{"derivedFrom":[subQ1,subQ0]});Q28=makeQuery(id+"F0.imprint","IMPRINT",FACE,{"disambiguationData":[TD([[makeQuery(id+"F0.imprint","IMPRINT",EDGE,{"disambiguationData":[TD([[subQ2,-1.0]])],"derivedFrom":subQ1}),-1.0]])]});}
            var Q29;
            {var subQ11=sQuery(id+"F0.wireOp",EDGE,"E7.right");Q29=makeQuery(id+"F0.imprint","IMPRINT",FACE,{"disambiguationData":[TD([[makeQuery(id+"F0.imprint","IMPRINT",EDGE,{"derivedFrom":subQ11}),-1.0]])]});}
            var Q30;
            {var subQ4=sQuery(id+"F0.wireOp",EDGE,"E8.left");Q30=makeQuery(id+"F0.imprint","IMPRINT",FACE,{"disambiguationData":[TD([[makeQuery(id+"F0.imprint","IMPRINT",EDGE,{"derivedFrom":subQ4}),1.0]])]});}
            var Q31;
            {var subQ0=sQuery(id+"F0.wireOp",EDGE,"E8.right");Q31=makeQuery(id+"F0.imprint","IMPRINT",FACE,{"disambiguationData":[TD([[makeQuery(id+"F0.imprint","IMPRINT",EDGE,{"derivedFrom":subQ0}),-1.0]])]});}
            var Q32;
            {var subQ0=sQuery(id+"F0.wireOp",EDGE,"E20.left");Q32=makeQuery(id+"F0.imprint","IMPRINT",FACE,{"disambiguationData":[TD([[makeQuery(id+"F0.imprint","IMPRINT",EDGE,{"derivedFrom":subQ0}),1.0]])]});}
            var Q33;
            {var subQ0=sQuery(id+"F0.wireOp",EDGE,"E26");Q33=makeQuery(id+"F0.imprint","IMPRINT",FACE,{"disambiguationData":[TD([[makeQuery(id+"F0.imprint","IMPRINT",EDGE,{"derivedFrom":subQ0}),1.0]])]});}
            var Q34;
            {var subQ0=sQuery(id+"F0.wireOp",EDGE,"E27");Q34=makeQuery(id+"F0.imprint","IMPRINT",FACE,{"disambiguationData":[TD([[makeQuery(id+"F0.imprint","IMPRINT",EDGE,{"derivedFrom":subQ0}),-1.0]])]});}
            var Q35;
            {var subQ0=sQuery(id+"F0.wireOp",EDGE,"E21.left");Q35=makeQuery(id+"F0.imprint","IMPRINT",FACE,{"disambiguationData":[TD([[makeQuery(id+"F0.imprint","IMPRINT",EDGE,{"derivedFrom":subQ0}),-1.0]])]});}
            extrude(context, id + "F5", {"entities" : qUnion([Q0, Q1, Q2, Q3, Q4, Q5, Q6, Q7, Q8, Q9, Q10, Q11, Q12, Q13, Q14, Q15, Q16, Q17, Q18, Q19, Q20, Q21, Q22, Q23, Q24, Q25, Q26, Q27, Q28, Q29, Q30, Q31, Q32, Q33, Q34, Q35]), "operationType" : NewBodyOperationType.ADD, "depth" : 2.54 * mm});
        }
        {
            var Q0;
            {var subQ0=sQuery(id+"F0.wireOp",EDGE,"E9.left");var subQ1=sQuery(id+"F0.wireOp",EDGE,"E8.bottom");var subQ2=makeQuery(id+"F0.imprint","INTERSECT",VERTEX,{"derivedFrom":[subQ1,subQ0]});Q0=makeQuery(id+"F0.imprint","IMPRINT",FACE,{"disambiguationData":[TD([[makeQuery(id+"F0.imprint","IMPRINT",EDGE,{"disambiguationData":[TD([[subQ2,-1.0]])],"derivedFrom":subQ1}),-1.0]])]});}
            var Q1;
            {var subQ5=sQuery(id+"F0.wireOp",EDGE,"E18.left");Q1=makeQuery(id+"F0.imprint","IMPRINT",FACE,{"disambiguationData":[TD([[makeQuery(id+"F0.imprint","IMPRINT",EDGE,{"derivedFrom":subQ5}),1.0]])]});}
            var Q2;
            {var subQ0=sQuery(id+"F0.wireOp",EDGE,"E9.left");var subQ1=sQuery(id+"F0.wireOp",EDGE,"E8.top");var subQ2=makeQuery(id+"F0.imprint","INTERSECT",VERTEX,{"derivedFrom":[subQ1,subQ0]});Q2=makeQuery(id+"F0.imprint","IMPRINT",FACE,{"disambiguationData":[TD([[makeQuery(id+"F0.imprint","IMPRINT",EDGE,{"disambiguationData":[TD([[subQ2,-1.0]])],"derivedFrom":subQ1}),1.0]])]});}
            var Q3;
            {var subQ0=sQuery(id+"F0.wireOp",EDGE,"E18.bottom");var subQ1=sQuery(id+"F0.wireOp",EDGE,"E9.right");var subQ2=makeQuery(id+"F0.imprint","INTERSECT",VERTEX,{"derivedFrom":[subQ1,subQ0]});Q3=makeQuery(id+"F0.imprint","IMPRINT",FACE,{"disambiguationData":[TD([[makeQuery(id+"F0.imprint","IMPRINT",EDGE,{"disambiguationData":[TD([[subQ2,-1.0]])],"derivedFrom":subQ1}),1.0]])]});}
            var Q4;
            {var subQ0=sQuery(id+"F0.wireOp",EDGE,"E10.1.0.1");var subQ1=sQuery(id+"F0.wireOp",EDGE,"E8.bottom");var subQ2=makeQuery(id+"F0.imprint","INTERSECT",VERTEX,{"derivedFrom":[subQ1,subQ0]});Q4=makeQuery(id+"F0.imprint","IMPRINT",FACE,{"disambiguationData":[TD([[makeQuery(id+"F0.imprint","IMPRINT",EDGE,{"disambiguationData":[TD([[subQ2,-1.0]])],"derivedFrom":subQ1}),-1.0]])]});}
            var Q5;
            {var subQ0=sQuery(id+"F0.wireOp",EDGE,"E18.bottom");var subQ1=sQuery(id+"F0.wireOp",EDGE,"E10.1.0.1");var subQ2=makeQuery(id+"F0.imprint","INTERSECT",VERTEX,{"derivedFrom":[subQ1,subQ0]});Q5=makeQuery(id+"F0.imprint","IMPRINT",FACE,{"disambiguationData":[TD([[makeQuery(id+"F0.imprint","IMPRINT",EDGE,{"disambiguationData":[TD([[subQ2,-1.0]])],"derivedFrom":subQ1}),1.0]])]});}
            var Q6;
            {var subQ0=sQuery(id+"F0.wireOp",EDGE,"E10.1.0.1");var subQ1=sQuery(id+"F0.wireOp",EDGE,"E8.top");var subQ2=makeQuery(id+"F0.imprint","INTERSECT",VERTEX,{"derivedFrom":[subQ1,subQ0]});Q6=makeQuery(id+"F0.imprint","IMPRINT",FACE,{"disambiguationData":[TD([[makeQuery(id+"F0.imprint","IMPRINT",EDGE,{"disambiguationData":[TD([[subQ2,-1.0]])],"derivedFrom":subQ1}),1.0]])]});}
            var Q7;
            {var subQ0=sQuery(id+"F0.wireOp",EDGE,"E18.bottom");var subQ1=sQuery(id+"F0.wireOp",EDGE,"E10.1.0.3");var subQ2=makeQuery(id+"F0.imprint","INTERSECT",VERTEX,{"derivedFrom":[subQ1,subQ0]});Q7=makeQuery(id+"F0.imprint","IMPRINT",FACE,{"disambiguationData":[TD([[makeQuery(id+"F0.imprint","IMPRINT",EDGE,{"disambiguationData":[TD([[subQ2,-1.0]])],"derivedFrom":subQ1}),1.0]])]});}
            var Q8;
            {var subQ0=sQuery(id+"F0.wireOp",EDGE,"E18.bottom");var subQ1=sQuery(id+"F0.wireOp",EDGE,"E10.2.0.1");var subQ2=makeQuery(id+"F0.imprint","INTERSECT",VERTEX,{"derivedFrom":[subQ1,subQ0]});Q8=makeQuery(id+"F0.imprint","IMPRINT",FACE,{"disambiguationData":[TD([[makeQuery(id+"F0.imprint","IMPRINT",EDGE,{"disambiguationData":[TD([[subQ2,-1.0]])],"derivedFrom":subQ1}),1.0]])]});}
            var Q9;
            {var subQ0=sQuery(id+"F0.wireOp",EDGE,"E10.2.0.1");var subQ1=sQuery(id+"F0.wireOp",EDGE,"E8.bottom");var subQ2=makeQuery(id+"F0.imprint","INTERSECT",VERTEX,{"derivedFrom":[subQ1,subQ0]});Q9=makeQuery(id+"F0.imprint","IMPRINT",FACE,{"disambiguationData":[TD([[makeQuery(id+"F0.imprint","IMPRINT",EDGE,{"disambiguationData":[TD([[subQ2,-1.0]])],"derivedFrom":subQ1}),-1.0]])]});}
            var Q10;
            {var subQ0=sQuery(id+"F0.wireOp",EDGE,"E10.2.0.1");var subQ1=sQuery(id+"F0.wireOp",EDGE,"E8.top");var subQ2=makeQuery(id+"F0.imprint","INTERSECT",VERTEX,{"derivedFrom":[subQ1,subQ0]});Q10=makeQuery(id+"F0.imprint","IMPRINT",FACE,{"disambiguationData":[TD([[makeQuery(id+"F0.imprint","IMPRINT",EDGE,{"disambiguationData":[TD([[subQ2,-1.0]])],"derivedFrom":subQ1}),1.0]])]});}
            var Q11;
            {var subQ0=sQuery(id+"F0.wireOp",EDGE,"E11.3.3.0");var subQ1=sQuery(id+"F0.wireOp",EDGE,"E8.bottom");var subQ2=makeQuery(id+"F0.imprint","INTERSECT",VERTEX,{"derivedFrom":[subQ1,subQ0]});Q11=makeQuery(id+"F0.imprint","IMPRINT",FACE,{"disambiguationData":[TD([[makeQuery(id+"F0.imprint","IMPRINT",EDGE,{"disambiguationData":[TD([[subQ2,-1.0]])],"derivedFrom":subQ1}),-1.0]])]});}
            var Q12;
            {var subQ0=sQuery(id+"F0.wireOp",EDGE,"E18.bottom");var subQ1=sQuery(id+"F0.wireOp",EDGE,"E10.2.0.3");var subQ2=makeQuery(id+"F0.imprint","INTERSECT",VERTEX,{"derivedFrom":[subQ1,subQ0]});Q12=makeQuery(id+"F0.imprint","IMPRINT",FACE,{"disambiguationData":[TD([[makeQuery(id+"F0.imprint","IMPRINT",EDGE,{"disambiguationData":[TD([[subQ2,-1.0]])],"derivedFrom":subQ1}),1.0]])]});}
            var Q13;
            {var subQ0=sQuery(id+"F0.wireOp",EDGE,"E18.bottom");var subQ1=sQuery(id+"F0.wireOp",EDGE,"E11.3.3.0");var subQ2=makeQuery(id+"F0.imprint","INTERSECT",VERTEX,{"derivedFrom":[subQ1,subQ0]});Q13=makeQuery(id+"F0.imprint","IMPRINT",FACE,{"disambiguationData":[TD([[makeQuery(id+"F0.imprint","IMPRINT",EDGE,{"disambiguationData":[TD([[subQ2,-1.0]])],"derivedFrom":subQ1}),1.0]])]});}
            var Q14;
            {var subQ0=sQuery(id+"F0.wireOp",EDGE,"E11.3.3.0");var subQ1=sQuery(id+"F0.wireOp",EDGE,"E8.top");var subQ2=makeQuery(id+"F0.imprint","INTERSECT",VERTEX,{"derivedFrom":[subQ1,subQ0]});Q14=makeQuery(id+"F0.imprint","IMPRINT",FACE,{"disambiguationData":[TD([[makeQuery(id+"F0.imprint","IMPRINT",EDGE,{"disambiguationData":[TD([[subQ2,-1.0]])],"derivedFrom":subQ1}),1.0]])]});}
            var Q15;
            {var subQ0=sQuery(id+"F0.wireOp",EDGE,"E11.3.4.0");var subQ1=sQuery(id+"F0.wireOp",EDGE,"E8.bottom");var subQ2=makeQuery(id+"F0.imprint","INTERSECT",VERTEX,{"derivedFrom":[subQ1,subQ0]});Q15=makeQuery(id+"F0.imprint","IMPRINT",FACE,{"disambiguationData":[TD([[makeQuery(id+"F0.imprint","IMPRINT",EDGE,{"disambiguationData":[TD([[subQ2,-1.0]])],"derivedFrom":subQ1}),-1.0]])]});}
            var Q16;
            {var subQ0=sQuery(id+"F0.wireOp",EDGE,"E18.bottom");var subQ1=sQuery(id+"F0.wireOp",EDGE,"E11.3.4.0");var subQ2=makeQuery(id+"F0.imprint","INTERSECT",VERTEX,{"derivedFrom":[subQ1,subQ0]});Q16=makeQuery(id+"F0.imprint","IMPRINT",FACE,{"disambiguationData":[TD([[makeQuery(id+"F0.imprint","IMPRINT",EDGE,{"disambiguationData":[TD([[subQ2,-1.0]])],"derivedFrom":subQ1}),1.0]])]});}
            var Q17;
            {var subQ0=sQuery(id+"F0.wireOp",EDGE,"E18.bottom");var subQ1=sQuery(id+"F0.wireOp",EDGE,"E11.9.3.0");var subQ2=makeQuery(id+"F0.imprint","INTERSECT",VERTEX,{"derivedFrom":[subQ1,subQ0]});Q17=makeQuery(id+"F0.imprint","IMPRINT",FACE,{"disambiguationData":[TD([[makeQuery(id+"F0.imprint","IMPRINT",EDGE,{"disambiguationData":[TD([[subQ2,-1.0]])],"derivedFrom":subQ1}),1.0]])]});}
            var Q18;
            {var subQ0=sQuery(id+"F0.wireOp",EDGE,"E11.3.4.0");var subQ1=sQuery(id+"F0.wireOp",EDGE,"E8.top");var subQ2=makeQuery(id+"F0.imprint","INTERSECT",VERTEX,{"derivedFrom":[subQ1,subQ0]});Q18=makeQuery(id+"F0.imprint","IMPRINT",FACE,{"disambiguationData":[TD([[makeQuery(id+"F0.imprint","IMPRINT",EDGE,{"disambiguationData":[TD([[subQ2,-1.0]])],"derivedFrom":subQ1}),1.0]])]});}
            var Q19;
            {var subQ0=sQuery(id+"F0.wireOp",EDGE,"E18.bottom");var subQ1=sQuery(id+"F0.wireOp",EDGE,"E11.9.4.0");var subQ2=makeQuery(id+"F0.imprint","INTERSECT",VERTEX,{"derivedFrom":[subQ1,subQ0]});Q19=makeQuery(id+"F0.imprint","IMPRINT",FACE,{"disambiguationData":[TD([[makeQuery(id+"F0.imprint","IMPRINT",EDGE,{"disambiguationData":[TD([[subQ2,-1.0]])],"derivedFrom":subQ1}),1.0]])]});}
            var Q20;
            {var subQ0=sQuery(id+"F0.wireOp",EDGE,"E11.3.5.0");var subQ1=sQuery(id+"F0.wireOp",EDGE,"E8.bottom");var subQ2=makeQuery(id+"F0.imprint","INTERSECT",VERTEX,{"derivedFrom":[subQ1,subQ0]});Q20=makeQuery(id+"F0.imprint","IMPRINT",FACE,{"disambiguationData":[TD([[makeQuery(id+"F0.imprint","IMPRINT",EDGE,{"disambiguationData":[TD([[subQ2,-1.0]])],"derivedFrom":subQ1}),-1.0]])]});}
            var Q21;
            {var subQ0=sQuery(id+"F0.wireOp",EDGE,"E18.bottom");var subQ1=sQuery(id+"F0.wireOp",EDGE,"E11.3.5.0");var subQ2=makeQuery(id+"F0.imprint","INTERSECT",VERTEX,{"derivedFrom":[subQ1,subQ0]});Q21=makeQuery(id+"F0.imprint","IMPRINT",FACE,{"disambiguationData":[TD([[makeQuery(id+"F0.imprint","IMPRINT",EDGE,{"disambiguationData":[TD([[subQ2,-1.0]])],"derivedFrom":subQ1}),1.0]])]});}
            var Q22;
            {var subQ0=sQuery(id+"F0.wireOp",EDGE,"E11.3.5.0");var subQ1=sQuery(id+"F0.wireOp",EDGE,"E8.top");var subQ2=makeQuery(id+"F0.imprint","INTERSECT",VERTEX,{"derivedFrom":[subQ1,subQ0]});Q22=makeQuery(id+"F0.imprint","IMPRINT",FACE,{"disambiguationData":[TD([[makeQuery(id+"F0.imprint","IMPRINT",EDGE,{"disambiguationData":[TD([[subQ2,-1.0]])],"derivedFrom":subQ1}),1.0]])]});}
            var Q23;
            {var subQ0=sQuery(id+"F0.wireOp",EDGE,"E11.3.6.0");var subQ1=sQuery(id+"F0.wireOp",EDGE,"E8.bottom");var subQ2=makeQuery(id+"F0.imprint","INTERSECT",VERTEX,{"derivedFrom":[subQ1,subQ0]});Q23=makeQuery(id+"F0.imprint","IMPRINT",FACE,{"disambiguationData":[TD([[makeQuery(id+"F0.imprint","IMPRINT",EDGE,{"disambiguationData":[TD([[subQ2,-1.0]])],"derivedFrom":subQ1}),-1.0]])]});}
            var Q24;
            {var subQ0=sQuery(id+"F0.wireOp",EDGE,"E18.bottom");var subQ1=sQuery(id+"F0.wireOp",EDGE,"E11.9.5.0");var subQ2=makeQuery(id+"F0.imprint","INTERSECT",VERTEX,{"derivedFrom":[subQ1,subQ0]});Q24=makeQuery(id+"F0.imprint","IMPRINT",FACE,{"disambiguationData":[TD([[makeQuery(id+"F0.imprint","IMPRINT",EDGE,{"disambiguationData":[TD([[subQ2,-1.0]])],"derivedFrom":subQ1}),1.0]])]});}
            var Q25;
            {var subQ0=sQuery(id+"F0.wireOp",EDGE,"E18.bottom");var subQ1=sQuery(id+"F0.wireOp",EDGE,"E11.3.6.0");var subQ2=makeQuery(id+"F0.imprint","INTERSECT",VERTEX,{"derivedFrom":[subQ1,subQ0]});Q25=makeQuery(id+"F0.imprint","IMPRINT",FACE,{"disambiguationData":[TD([[makeQuery(id+"F0.imprint","IMPRINT",EDGE,{"disambiguationData":[TD([[subQ2,-1.0]])],"derivedFrom":subQ1}),1.0]])]});}
            var Q26;
            {var subQ0=sQuery(id+"F0.wireOp",EDGE,"E11.3.6.0");var subQ1=sQuery(id+"F0.wireOp",EDGE,"E8.top");var subQ2=makeQuery(id+"F0.imprint","INTERSECT",VERTEX,{"derivedFrom":[subQ1,subQ0]});Q26=makeQuery(id+"F0.imprint","IMPRINT",FACE,{"disambiguationData":[TD([[makeQuery(id+"F0.imprint","IMPRINT",EDGE,{"disambiguationData":[TD([[subQ2,-1.0]])],"derivedFrom":subQ1}),1.0]])]});}
            var Q27;
            {var subQ0=sQuery(id+"F0.wireOp",EDGE,"E11.3.7.0");var subQ1=sQuery(id+"F0.wireOp",EDGE,"E8.bottom");var subQ2=makeQuery(id+"F0.imprint","INTERSECT",VERTEX,{"derivedFrom":[subQ1,subQ0]});Q27=makeQuery(id+"F0.imprint","IMPRINT",FACE,{"disambiguationData":[TD([[makeQuery(id+"F0.imprint","IMPRINT",EDGE,{"disambiguationData":[TD([[subQ2,-1.0]])],"derivedFrom":subQ1}),-1.0]])]});}
            var Q28;
            {var subQ0=sQuery(id+"F0.wireOp",EDGE,"E18.bottom");var subQ1=sQuery(id+"F0.wireOp",EDGE,"E11.9.6.0");var subQ2=makeQuery(id+"F0.imprint","INTERSECT",VERTEX,{"derivedFrom":[subQ1,subQ0]});Q28=makeQuery(id+"F0.imprint","IMPRINT",FACE,{"disambiguationData":[TD([[makeQuery(id+"F0.imprint","IMPRINT",EDGE,{"disambiguationData":[TD([[subQ2,-1.0]])],"derivedFrom":subQ1}),1.0]])]});}
            var Q29;
            {var subQ5=sQuery(id+"F0.wireOp",EDGE,"E18.right");Q29=makeQuery(id+"F0.imprint","IMPRINT",FACE,{"disambiguationData":[TD([[makeQuery(id+"F0.imprint","IMPRINT",EDGE,{"derivedFrom":subQ5}),-1.0]])]});}
            var Q30;
            {var subQ0=sQuery(id+"F0.wireOp",EDGE,"E11.3.7.0");var subQ1=sQuery(id+"F0.wireOp",EDGE,"E8.top");var subQ2=makeQuery(id+"F0.imprint","INTERSECT",VERTEX,{"derivedFrom":[subQ1,subQ0]});Q30=makeQuery(id+"F0.imprint","IMPRINT",FACE,{"disambiguationData":[TD([[makeQuery(id+"F0.imprint","IMPRINT",EDGE,{"disambiguationData":[TD([[subQ2,-1.0]])],"derivedFrom":subQ1}),1.0]])]});}
            extrude(context, id + "F6", {"entities" : qUnion([Q0, Q1, Q2, Q3, Q4, Q5, Q6, Q7, Q8, Q9, Q10, Q11, Q12, Q13, Q14, Q15, Q16, Q17, Q18, Q19, Q20, Q21, Q22, Q23, Q24, Q25, Q26, Q27, Q28, Q29, Q30]), "operationType" : NewBodyOperationType.REMOVE, "oppositeDirection" : true, "depth" : 0.5 * mm});
        }
        {
            var Q0;
            {var subQ0=sQuery(id+"F0.wireOp",EDGE,"E20.right");Q0=makeQuery(id+"F0.imprint","IMPRINT",FACE,{"disambiguationData":[TD([[makeQuery(id+"F0.imprint","IMPRINT",EDGE,{"derivedFrom":subQ0}),-1.0]])]});}
            var Q1;
            {var subQ0=sQuery(id+"F0.wireOp",EDGE,"E21.right");Q1=makeQuery(id+"F0.imprint","IMPRINT",FACE,{"disambiguationData":[TD([[makeQuery(id+"F0.imprint","IMPRINT",EDGE,{"derivedFrom":subQ0}),1.0]])]});}
            var Q2;
            Q2=makeQuery(id+"F0.imprint","IMPRINT",FACE,{"disambiguationData":[TD([[makeQuery(id+"F0.imprint","IMPRINT",EDGE,{"derivedFrom":sQuery(id+"F0.wireOp",EDGE,"E17")}),-1.0]])]});
            var Q3;
            Q3=makeQuery(id+"F0.imprint","IMPRINT",FACE,{"disambiguationData":[TD([[makeQuery(id+"F0.imprint","IMPRINT",EDGE,{"derivedFrom":sQuery(id+"F0.wireOp",EDGE,"E16")}),-1.0]])]});
            var Q4;
            Q4=makeQuery(id+"F0.imprint","IMPRINT",FACE,{"disambiguationData":[TD([[makeQuery(id+"F0.imprint","IMPRINT",EDGE,{"derivedFrom":sQuery(id+"F0.wireOp",EDGE,"E16")}),1.0]])]});
            var Q5;
            Q5=makeQuery(id+"F0.imprint","IMPRINT",FACE,{"disambiguationData":[TD([[makeQuery(id+"F0.imprint","IMPRINT",EDGE,{"derivedFrom":sQuery(id+"F0.wireOp",EDGE,"E17")}),1.0]])]});
            var Q6;
            Q6=makeQuery(id+"F0.imprint","IMPRINT",FACE,{"disambiguationData":[TD([[makeQuery(id+"F0.imprint","IMPRINT",EDGE,{"derivedFrom":sQuery(id+"F0.wireOp",EDGE,"E30")}),1.0]])]});
            var Q7;
            Q7=makeQuery(id+"F0.imprint","IMPRINT",FACE,{"disambiguationData":[TD([[makeQuery(id+"F0.imprint","IMPRINT",EDGE,{"derivedFrom":sQuery(id+"F0.wireOp",EDGE,"E31")}),1.0]])]});
            extrude(context, id + "F7", {"entities" : qUnion([Q0, Q1, Q2, Q3, Q4, Q5, Q6, Q7]), "operationType" : NewBodyOperationType.ADD, "depth" : 3.8 * mm});
        }
        {
            var Q0;
            Q0=makeQuery(id+"F0.imprint","IMPRINT",FACE,{"disambiguationData":[TD([[makeQuery(id+"F0.imprint","IMPRINT",EDGE,{"derivedFrom":sQuery(id+"F0.wireOp",EDGE,"E30")}),1.0]])]});
            var Q1;
            Q1=makeQuery(id+"F0.imprint","IMPRINT",FACE,{"disambiguationData":[TD([[makeQuery(id+"F0.imprint","IMPRINT",EDGE,{"derivedFrom":sQuery(id+"F0.wireOp",EDGE,"E31")}),1.0]])]});
            var Q2;
            Q2=makeQuery(id+"F0.imprint","IMPRINT",FACE,{"disambiguationData":[TD([[makeQuery(id+"F0.imprint","IMPRINT",EDGE,{"derivedFrom":sQuery(id+"F0.wireOp",EDGE,"E17")}),1.0]])]});
            var Q3;
            Q3=makeQuery(id+"F0.imprint","IMPRINT",FACE,{"disambiguationData":[TD([[makeQuery(id+"F0.imprint","IMPRINT",EDGE,{"derivedFrom":sQuery(id+"F0.wireOp",EDGE,"E16")}),1.0]])]});
            extrude(context, id + "F8", {"entities" : qUnion([Q0, Q1, Q2, Q3]), "operationType" : NewBodyOperationType.REMOVE, "depth" : 3.8 * mm, "hasSecondDirection" : true, "secondDirectionOppositeDirection" : true, "secondDirectionDepth" : 3.8 * mm});
        }
    });
